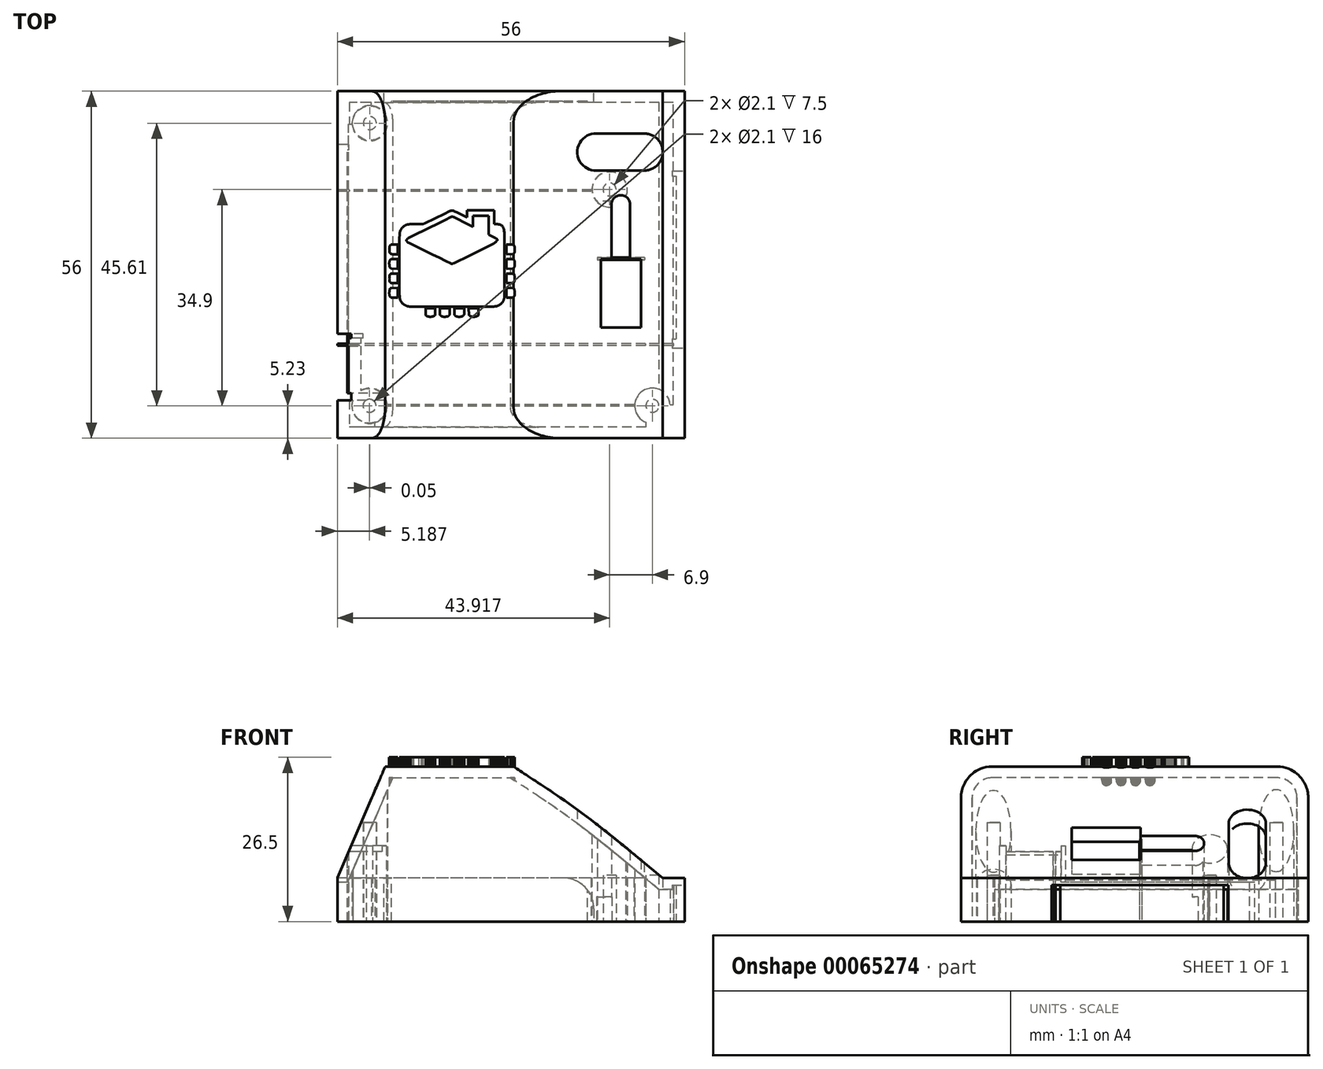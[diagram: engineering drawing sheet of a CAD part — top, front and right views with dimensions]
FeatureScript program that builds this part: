
annotation { "Feature Type Name" : "Feature", "Feature Type Description" : "" }
export const myFeature = defineFeature(function(context is Context, id is Id, definition is map)
    precondition{}
    {
        {
            var Q0;
            Q0=qCreatedBy(makeId("Top.planeOp"),FACE);
            var sketch = newSketch(context, id + "F0", { "sketchPlane" : qUnion([Q0])});
            skLineSegment(sketch, "E0.rect.bottom", {"start": v(22.84, -21.13) * mm, "end": v(-26.83, -21.13) * mm});
            skLineSegment(sketch, "E0.rect.top", {"start": v(22.84, 28.7) * mm, "end": v(-26.83, 28.7) * mm});
            skLineSegment(sketch, "E0.rect.left", {"start": v(22.84, -21.13) * mm, "end": v(22.84, 28.7) * mm});
            skPoint(sketch, "E0.rect.middle", {"position": v(-2, 3.78) * mm});
            skCircle(sketch, "E1", {"center": v(-24.81, -18.99) * mm, "radius": 1.05 * mm});
            skCircle(sketch, "E2", {"center": v(-24.76, 26.62) * mm, "radius": 1.05 * mm});
            skCircle(sketch, "E3", {"center": v(13.92, 15.91) * mm, "radius": 1.05 * mm});
            skLineSegment(sketch, "E4", {"start": v(-2, -21.13) * mm, "end": v(-2, -18.21) * mm});
            skCircle(sketch, "E5.MirrorC", {"center": v(20.82, -18.99) * mm, "radius": 1.05 * mm});
            skLineSegment(sketch, "E6.rect.bottom", {"start": v(24.75, -22.97) * mm, "end": v(-28.75, -22.97) * mm});
            skLineSegment(sketch, "E6.rect.top", {"start": v(24.75, 30.53) * mm, "end": v(-28.75, 30.53) * mm});
            skLineSegment(sketch, "E6.rect.left", {"start": v(24.75, -22.97) * mm, "end": v(24.75, 30.53) * mm});
            skLineSegment(sketch, "E6.rect.right", {"start": v(-28.75, -22.97) * mm, "end": v(-28.75, 30.53) * mm});
            skLineSegment(sketch, "E7.rect.bottom", {"start": v(26, -24.22) * mm, "end": v(-30, -24.22) * mm});
            skLineSegment(sketch, "E7.rect.top", {"start": v(26, 31.78) * mm, "end": v(-30, 31.78) * mm});
            skLineSegment(sketch, "E7.rect.left", {"start": v(26, -24.22) * mm, "end": v(26, 31.78) * mm});
            skLineSegment(sketch, "E7.rect.right", {"start": v(-30, -24.22) * mm, "end": v(-30, 31.78) * mm});
            skPoint(sketch, "E8", {"position": v(8.65, 14) * mm});
            skSolve(sketch);
        }
        {
            var Q0;
            Q0=qSketchRegion(id+"F0",true);
            var Q1;
            Q1=makeQuery(id+"F0.imprint","IMPRINT",FACE,{"disambiguationData":[TD([[makeQuery(id+"F0.imprint","IMPRINT",EDGE,{"derivedFrom":sQuery(id+"F0.wireOp",EDGE,"E1")}),-1.0]])]});
            extrude(context, id + "F1", {"entities" : qUnion([Q0, Q1]), "depth" : 25 * mm});
        }
        {
            var Q0;
            Q0=qCreatedBy(makeId("Front.planeOp"),FACE);
            var sketch = newSketch(context, id + "F2", { "sketchPlane" : qUnion([Q0])});
            skLineSegment(sketch, "E9", {"start": v(0, 0) * mm, "end": v(0, 7) * mm});
            skLineSegment(sketch, "E10", {"start": v(0, 7) * mm, "end": v(26.03, 7) * mm});
            skLineSegment(sketch, "E11", {"start": v(26.03, 7) * mm, "end": v(26.03, 25.51) * mm});
            skLineSegment(sketch, "E12", {"start": v(15.3, 7) * mm, "end": v(26.03, 7) * mm});
            skLineSegment(sketch, "E13", {"start": v(0, 7) * mm, "end": v(-30.02, 7) * mm});
            skLineSegment(sketch, "E14", {"start": v(-30.02, 7) * mm, "end": v(-22.06, 25.51) * mm});
            skLineSegment(sketch, "E15", {"start": v(-22.06, 25.51) * mm, "end": v(-2.39, 25.51) * mm});
            skFitSpline(sketch, "E16", {"points": [v(-2.39, 25.51) * mm, v(9.33, 17.59) * mm, v(22.47, 7) * mm], "startDerivative": vector(24.35, -15.7) * mm, "endDerivative": vector(25.35, -21.24) * mm});
            skLineSegment(sketch, "E17", {"start": v(26.03, 25.51) * mm, "end": v(-2.39, 25.51) * mm});
            skLineSegment(sketch, "E18", {"start": v(-22.06, 25.51) * mm, "end": v(-30.02, 25.51) * mm});
            skLineSegment(sketch, "E19", {"start": v(-30.02, 25.51) * mm, "end": v(-30.02, 7) * mm});
            skSolve(sketch);
        }
        {
            var Q0;
            Q0=makeQuery(id+"F2.imprint","IMPRINT",FACE,{"disambiguationData":[TD([[makeQuery(id+"F2.imprint","IMPRINT",EDGE,{"derivedFrom":sQuery(id+"F2.wireOp",EDGE,"E14")}),1.0]])]});
            var Q1;
            {var subQ0=sQuery(id+"F2.wireOp",EDGE,"E11");Q1=makeQuery(id+"F2.imprint","IMPRINT",FACE,{"disambiguationData":[TD([[makeQuery(id+"F2.imprint","IMPRINT",EDGE,{"derivedFrom":subQ0}),1.0]])]});}
            extrude(context, id + "F3", {"entities" : qUnion([Q0, Q1]), "operationType" : NewBodyOperationType.REMOVE, "endBound" : BoundingType.UP_TO_NEXT, "oppositeDirection" : true, "depth" : 25 * mm, "hasSecondDirection" : true, "secondDirectionOppositeDirection" : false, "secondDirectionDepth" : 25 * mm});
        }
        {
            var Q0;
            Q0=makeQuery(id+"F1.opExtrude","CAP_EDGE",EDGE,{"disambiguationData":[OSD([sQuery(id+"F0.wireOp",EDGE,"E7.rect.right")])],"isStart":false});
            var Q1;
            Q1=makeQuery(id+"F3.boolean.opBoolean","COPY",EDGE,{"derivedFrom":makeQuery(id+"F3.opExtrude","TWEAK_EDGE",EDGE,{"derivedFrom":[makeQuery(id+"F1.opExtrude","CAP_FACE",FACE,{"disambiguationData":[OSD([sQuery(id+"F0.wireOp",EDGE,"E1"),sQuery(id+"F0.wireOp",EDGE,"E2"),sQuery(id+"F0.wireOp",EDGE,"E3"),sQuery(id+"F0.wireOp",EDGE,"E5.MirrorC"),sQuery(id+"F0.wireOp",EDGE,"E7.rect.bottom"),sQuery(id+"F0.wireOp",EDGE,"E7.rect.top"),sQuery(id+"F0.wireOp",EDGE,"E7.rect.left"),sQuery(id+"F0.wireOp",EDGE,"E7.rect.right")])],"isStart":false}),makeQuery(id+"F2.imprint","IMPRINT",EDGE,{"derivedFrom":sQuery(id+"F2.wireOp",EDGE,"ff17f17f-c23f-4b7b-92e3-773d52701edb")})]})});
            var Q2;
            Q2=makeQuery(id+"F3.boolean.opBoolean","COPY",EDGE,{"derivedFrom":makeQuery(id+"F3.opExtrude","TWEAK_EDGE",EDGE,{"derivedFrom":[makeQuery(id+"F1.opExtrude","CAP_FACE",FACE,{"disambiguationData":[OSD([sQuery(id+"F0.wireOp",EDGE,"E1"),sQuery(id+"F0.wireOp",EDGE,"E2"),sQuery(id+"F0.wireOp",EDGE,"E3"),sQuery(id+"F0.wireOp",EDGE,"E5.MirrorC"),sQuery(id+"F0.wireOp",EDGE,"E7.rect.bottom"),sQuery(id+"F0.wireOp",EDGE,"E7.rect.top"),sQuery(id+"F0.wireOp",EDGE,"E7.rect.left"),sQuery(id+"F0.wireOp",EDGE,"E7.rect.right")])],"isStart":false}),makeQuery(id+"F2.imprint","IMPRINT",EDGE,{"derivedFrom":sQuery(id+"F2.wireOp",EDGE,"7c30f75c-de24-4105-9ec6-0528e7197d9e")})]})});
            var Q3;
            {var subQ0=sQuery(id+"F2.wireOp",EDGE,"cpQ2IQLn-lepx-jHqE-Occg-QwCyzWVKbBFz");var subQ1=sQuery(id+"F2.wireOp",EDGE,"9136473a-ce9f-4df1-8e41-d79c079f6f02");var subQ2=makeQuery(id+"F2.imprint","INTERSECT",VERTEX,{"disambiguationData":[OD(0.0)],"derivedFrom":[subQ1,subQ0]});var subQ4=makeQuery(id+"F2.imprint","INTERSECT",VERTEX,{"disambiguationData":[OD(1.0)],"derivedFrom":[subQ1,subQ0]});Q3=makeQuery(id+"F3.boolean.opBoolean","COPY",EDGE,{"derivedFrom":makeQuery(id+"F3.opExtrude","TWEAK_EDGE",EDGE,{"derivedFrom":[makeQuery(id+"F1.opExtrude","CAP_FACE",FACE,{"disambiguationData":[OSD([sQuery(id+"F0.wireOp",EDGE,"E1"),sQuery(id+"F0.wireOp",EDGE,"E2"),sQuery(id+"F0.wireOp",EDGE,"E3"),sQuery(id+"F0.wireOp",EDGE,"E5.MirrorC"),sQuery(id+"F0.wireOp",EDGE,"E7.rect.bottom"),sQuery(id+"F0.wireOp",EDGE,"E7.rect.top"),sQuery(id+"F0.wireOp",EDGE,"E7.rect.left"),sQuery(id+"F0.wireOp",EDGE,"E7.rect.right")])],"isStart":false}),makeQuery(id+"F2.imprint","IMPRINT",EDGE,{"disambiguationData":[TD([[subQ4,1.0]])],"derivedFrom":subQ0}),makeQuery(id+"F2.imprint","IMPRINT",EDGE,{"disambiguationData":[TD([[subQ2,1.0]])],"derivedFrom":subQ0}),makeQuery(id+"F2.imprint","IMPRINT",EDGE,{"disambiguationData":[TD([[subQ2,-1.0]])],"derivedFrom":subQ0})]})});}
            var Q4;
            {var subQ0=sQuery(id+"F2.wireOp",EDGE,"cpQ2IQLn-lepx-jHqE-Occg-QwCyzWVKbBFz");var subQ1=sQuery(id+"F2.wireOp",EDGE,"9136473a-ce9f-4df1-8e41-d79c079f6f02");var subQ2=makeQuery(id+"F2.imprint","INTERSECT",VERTEX,{"disambiguationData":[OD(0.0)],"derivedFrom":[subQ1,subQ0]});var subQ3=sQuery(id+"F2.wireOp",EDGE,"7c30f75c-de24-4105-9ec6-0528e7197d9e");var subQ4=makeQuery(id+"F2.imprint","INTERSECT",VERTEX,{"derivedFrom":[subQ3,subQ0]});var subQ5=makeQuery(id+"F2.imprint","INTERSECT",VERTEX,{"disambiguationData":[OD(1.0)],"derivedFrom":[subQ1,subQ0]});Q4=makeQuery(id+"F3.boolean.opBoolean","COPY",EDGE,{"derivedFrom":makeQuery(id+"F3.opExtrude","TWEAK_EDGE",EDGE,{"disambiguationData":[OD(0.0)],"derivedFrom":[makeQuery(id+"F2.imprint","IMPRINT",EDGE,{"disambiguationData":[TD([[subQ4,1.0]])],"derivedFrom":subQ3}),makeQuery(id+"F2.imprint","IMPRINT",EDGE,{"disambiguationData":[TD([[subQ5,1.0]])],"derivedFrom":subQ0}),makeQuery(id+"F2.imprint","IMPRINT",EDGE,{"disambiguationData":[TD([[subQ2,1.0]])],"derivedFrom":subQ0}),makeQuery(id+"F2.imprint","IMPRINT",EDGE,{"disambiguationData":[TD([[subQ2,-1.0]])],"derivedFrom":subQ0})]})});}
            var Q5;
            {var subQ0=sQuery(id+"F2.wireOp",EDGE,"cpQ2IQLn-lepx-jHqE-Occg-QwCyzWVKbBFz");var subQ1=sQuery(id+"F2.wireOp",EDGE,"9136473a-ce9f-4df1-8e41-d79c079f6f02");var subQ2=makeQuery(id+"F2.imprint","INTERSECT",VERTEX,{"disambiguationData":[OD(0.0)],"derivedFrom":[subQ1,subQ0]});var subQ3=sQuery(id+"F2.wireOp",EDGE,"7c30f75c-de24-4105-9ec6-0528e7197d9e");var subQ4=makeQuery(id+"F2.imprint","INTERSECT",VERTEX,{"derivedFrom":[subQ3,subQ0]});var subQ5=makeQuery(id+"F2.imprint","INTERSECT",VERTEX,{"disambiguationData":[OD(1.0)],"derivedFrom":[subQ1,subQ0]});Q5=makeQuery(id+"F3.boolean.opBoolean","COPY",EDGE,{"derivedFrom":makeQuery(id+"F3.opExtrude","TWEAK_EDGE",EDGE,{"disambiguationData":[OD(1.0)],"derivedFrom":[makeQuery(id+"F2.imprint","IMPRINT",EDGE,{"disambiguationData":[TD([[subQ4,1.0]])],"derivedFrom":subQ3}),makeQuery(id+"F2.imprint","IMPRINT",EDGE,{"disambiguationData":[TD([[subQ5,1.0]])],"derivedFrom":subQ0}),makeQuery(id+"F2.imprint","IMPRINT",EDGE,{"disambiguationData":[TD([[subQ2,1.0]])],"derivedFrom":subQ0}),makeQuery(id+"F2.imprint","IMPRINT",EDGE,{"disambiguationData":[TD([[subQ2,-1.0]])],"derivedFrom":subQ0})]})});}
            var Q6;
            Q6=makeQuery(id+"F1.opExtrude","CAP_EDGE",EDGE,{"disambiguationData":[OSD([sQuery(id+"F0.wireOp",EDGE,"E7.rect.bottom")])],"isStart":false});
            var Q7;
            {var subQ0=sQuery(id+"F2.wireOp",EDGE,"cpQ2IQLn-lepx-jHqE-Occg-QwCyzWVKbBFz");var subQ1=sQuery(id+"F2.wireOp",EDGE,"9136473a-ce9f-4df1-8e41-d79c079f6f02");var subQ2=makeQuery(id+"F2.imprint","INTERSECT",VERTEX,{"disambiguationData":[OD(0.0)],"derivedFrom":[subQ1,subQ0]});var subQ4=makeQuery(id+"F2.imprint","INTERSECT",VERTEX,{"disambiguationData":[OD(1.0)],"derivedFrom":[subQ1,subQ0]});Q7=makeQuery(id+"F3.boolean.opBoolean","COPY",EDGE,{"derivedFrom":makeQuery(id+"F3.opExtrude","TWEAK_EDGE",EDGE,{"derivedFrom":[makeQuery(id+"F1.opExtrude","SWEPT_FACE",FACE,{"disambiguationData":[OSD([sQuery(id+"F0.wireOp",EDGE,"E7.rect.bottom")])]}),makeQuery(id+"F2.imprint","IMPRINT",EDGE,{"disambiguationData":[TD([[subQ4,1.0]])],"derivedFrom":subQ0}),makeQuery(id+"F2.imprint","IMPRINT",EDGE,{"disambiguationData":[TD([[subQ2,1.0]])],"derivedFrom":subQ0}),makeQuery(id+"F2.imprint","IMPRINT",EDGE,{"disambiguationData":[TD([[subQ2,-1.0]])],"derivedFrom":subQ0})]})});}
            var Q8;
            Q8=makeQuery(id+"F1.opExtrude","CAP_EDGE",EDGE,{"disambiguationData":[OSD([sQuery(id+"F0.wireOp",EDGE,"E7.rect.top")])],"isStart":false});
            var Q9;
            {var subQ0=sQuery(id+"F2.wireOp",EDGE,"cpQ2IQLn-lepx-jHqE-Occg-QwCyzWVKbBFz");var subQ1=sQuery(id+"F2.wireOp",EDGE,"9136473a-ce9f-4df1-8e41-d79c079f6f02");var subQ2=makeQuery(id+"F2.imprint","INTERSECT",VERTEX,{"disambiguationData":[OD(0.0)],"derivedFrom":[subQ1,subQ0]});var subQ4=makeQuery(id+"F2.imprint","INTERSECT",VERTEX,{"disambiguationData":[OD(1.0)],"derivedFrom":[subQ1,subQ0]});Q9=makeQuery(id+"F3.boolean.opBoolean","COPY",EDGE,{"derivedFrom":makeQuery(id+"F3.opExtrude","TWEAK_EDGE",EDGE,{"derivedFrom":[makeQuery(id+"F1.opExtrude","SWEPT_FACE",FACE,{"disambiguationData":[OSD([sQuery(id+"F0.wireOp",EDGE,"E7.rect.top")])]}),makeQuery(id+"F2.imprint","IMPRINT",EDGE,{"disambiguationData":[TD([[subQ4,1.0]])],"derivedFrom":subQ0}),makeQuery(id+"F2.imprint","IMPRINT",EDGE,{"disambiguationData":[TD([[subQ2,1.0]])],"derivedFrom":subQ0}),makeQuery(id+"F2.imprint","IMPRINT",EDGE,{"disambiguationData":[TD([[subQ2,-1.0]])],"derivedFrom":subQ0})]})});}
            var Q10;
            Q10=makeQuery(id+"F3.boolean.opBoolean","COPY",EDGE,{"derivedFrom":makeQuery(id+"F3.opExtrude","CAP_EDGE",EDGE,{"disambiguationData":[OSD([sQuery(id+"F2.wireOp",EDGE,"E16")]),topologyDisambiguationEdgeConnected([makeQuery(id+"F1.opExtrude","CAP_FACE",FACE,{"disambiguationData":[OSD([sQuery(id+"F0.wireOp",EDGE,"E1"),sQuery(id+"F0.wireOp",EDGE,"E2"),sQuery(id+"F0.wireOp",EDGE,"E3"),sQuery(id+"F0.wireOp",EDGE,"E5.MirrorC"),sQuery(id+"F0.wireOp",EDGE,"E7.rect.bottom"),sQuery(id+"F0.wireOp",EDGE,"E7.rect.top"),sQuery(id+"F0.wireOp",EDGE,"E7.rect.left"),sQuery(id+"F0.wireOp",EDGE,"E7.rect.right")])],"isStart":false})])],"isStart":false})});
            var Q11;
            {var subQ0=sQuery(id+"F2.wireOp",EDGE,"E14");Q11=makeQuery(id+"F3.boolean.opBoolean","COPY",EDGE,{"derivedFrom":makeQuery(id+"F3.opExtrude","CAP_EDGE",EDGE,{"disambiguationData":[OSD([subQ0]),topologyDisambiguationEdgeConnected([makeQuery(id+"F1.opExtrude","CAP_FACE",FACE,{"disambiguationData":[OSD([sQuery(id+"F0.wireOp",EDGE,"E1"),sQuery(id+"F0.wireOp",EDGE,"E2"),sQuery(id+"F0.wireOp",EDGE,"E3"),sQuery(id+"F0.wireOp",EDGE,"E5.MirrorC"),sQuery(id+"F0.wireOp",EDGE,"E7.rect.bottom"),sQuery(id+"F0.wireOp",EDGE,"E7.rect.top"),sQuery(id+"F0.wireOp",EDGE,"E7.rect.left"),sQuery(id+"F0.wireOp",EDGE,"E7.rect.right")])],"isStart":false})])],"isStart":false})});}
            fillet(context, id + "F4", {"entities" : qUnion([Q0, Q1, Q2, Q3, Q4, Q5, Q6, Q7, Q8, Q9, Q10, Q11]), "radius" : 5 * mm, "tangentPropagation" : true, "allowEdgeOverflow" : false});
        }
        {
            var Q0;
            Q0=makeQuery(id+"F1.opExtrude","SWEPT_BODY",BODY,{"disambiguationData":[OSD([sQuery(id+"F0.wireOp",EDGE,"E1"),sQuery(id+"F0.wireOp",EDGE,"E2"),sQuery(id+"F0.wireOp",EDGE,"E3"),sQuery(id+"F0.wireOp",EDGE,"E5.MirrorC"),sQuery(id+"F0.wireOp",EDGE,"E7.rect.bottom"),sQuery(id+"F0.wireOp",EDGE,"E7.rect.top"),sQuery(id+"F0.wireOp",EDGE,"E7.rect.left"),sQuery(id+"F0.wireOp",EDGE,"E7.rect.right")])]});
            transform(context, id + "F5", {"entities" : qUnion([Q0]), "transformType" : TransformType.TRANSLATION_3D, "dx" : -5 * mm, "dy" : -12 * mm, "dz" : 0 * mm, "makeCopy" : false});
        }
        {
            var Q0;
            Q0=makeQuery(id+"F1.opExtrude","CAP_FACE",FACE,{"disambiguationData":[OSD([sQuery(id+"F0.wireOp",EDGE,"E1"),sQuery(id+"F0.wireOp",EDGE,"E2"),sQuery(id+"F0.wireOp",EDGE,"E3"),sQuery(id+"F0.wireOp",EDGE,"E5.MirrorC"),sQuery(id+"F0.wireOp",EDGE,"E7.rect.bottom"),sQuery(id+"F0.wireOp",EDGE,"E7.rect.top"),sQuery(id+"F0.wireOp",EDGE,"E7.rect.left"),sQuery(id+"F0.wireOp",EDGE,"E7.rect.right")])],"isStart":true});
            shell(context, id + "F6", {"entities" : qUnion([Q0]), "thickness" : 1.8 * mm});
        }
        {
            var Q0;
            Q0=makeQuery(id+"F1.opExtrude","SWEPT_FACE",FACE,{"disambiguationData":[OSD([sQuery(id+"F0.wireOp",EDGE,"E7.rect.left")])]});
            cPlane(context, id + "F7", {"entities" : qUnion([Q0]), "cplaneType" : CPlaneType.OFFSET, "offset" : 0 * mm, "width" : 150 * mm, "height" : 150 * mm});
        }
        {
            var Q0;
            Q0=qCreatedBy(id+"F7.planeOp",FACE);
            var sketch = newSketch(context, id + "F8", { "sketchPlane" : qUnion([Q0])});
            skLineSegment(sketch, "E20.bottom", {"start": v(6.92, 0) * mm, "end": v(-20.2, 0) * mm});
            skLineSegment(sketch, "E20.top", {"start": v(6.92, 5.87) * mm, "end": v(-20.2, 5.87) * mm});
            skLineSegment(sketch, "E21", {"start": v(-20.2, 5.87) * mm, "end": v(-21.64, 5.87) * mm});
            skLineSegment(sketch, "E22", {"start": v(-21.64, 5.87) * mm, "end": v(-21.64, 0) * mm});
            skLineSegment(sketch, "E23", {"start": v(-21.64, 0) * mm, "end": v(-20.2, 0) * mm});
            skLineSegment(sketch, "E24", {"start": v(-20.2, 5.87) * mm, "end": v(-20.2, 0) * mm});
            skLineSegment(sketch, "E25", {"start": v(6.92, 0) * mm, "end": v(6.92, 5.87) * mm});
            skLineSegment(sketch, "E26", {"start": v(6.12, 5.87) * mm, "end": v(6.12, 0) * mm});
            skPoint(sketch, "E27.orphan", {"position": v(7.84, 0) * mm});
            skSolve(sketch);
        }
        {
            var Q0;
            Q0=qSketchRegion(id+"F8",true);
            extrude(context, id + "F9", {"entities" : qUnion([Q0]), "operationType" : NewBodyOperationType.REMOVE, "oppositeDirection" : true, "depth" : (1.7 - 0.3) * mm});
        }
        {
            var Q0;
            Q0=makeQuery(id+"F8.imprint","IMPRINT",FACE,{"disambiguationData":[TD([[makeQuery(id+"F8.imprint","IMPRINT",EDGE,{"derivedFrom":sQuery(id+"F8.wireOp",EDGE,"E21")}),1.0]])]});
            var Q1;
            {var subQ0=sQuery(id+"F8.wireOp",EDGE,"E20.left");Q1=makeQuery(id+"F8.imprint","IMPRINT",FACE,{"disambiguationData":[TD([[makeQuery(id+"F8.imprint","IMPRINT",EDGE,{"derivedFrom":subQ0}),1.0]])]});}
            var Q2;
            {var subQ0=sQuery(id+"F8.wireOp",EDGE,"E25");Q2=makeQuery(id+"F8.imprint","IMPRINT",FACE,{"disambiguationData":[TD([[makeQuery(id+"F8.imprint","IMPRINT",EDGE,{"derivedFrom":subQ0}),1.0]])]});}
            extrude(context, id + "F10", {"entities" : qUnion([Q0, Q1, Q2]), "operationType" : NewBodyOperationType.REMOVE, "oppositeDirection" : true, "depth" : 2 * mm});
        }
        {
            var Q0;
            Q0=makeQuery(id+"F1.opExtrude","SWEPT_FACE",FACE,{"disambiguationData":[OSD([sQuery(id+"F0.wireOp",EDGE,"E7.rect.right")])]});
            cPlane(context, id + "F11", {"entities" : qUnion([Q0]), "cplaneType" : CPlaneType.OFFSET, "offset" : 0 * mm, "width" : 150 * mm, "height" : 150 * mm});
        }
        {
            var Q0;
            Q0=qCreatedBy(id+"F11.planeOp",FACE);
            var sketch = newSketch(context, id + "F12", { "sketchPlane" : qUnion([Q0])});
            skLineSegment(sketch, "E28.top", {"start": v(-11.15, 6.31) * mm, "end": v(19.35, 6.31) * mm});
            skLineSegment(sketch, "E29", {"start": v(27.25, 11.15) * mm, "end": v(27.25, 11.15) * mm});
            skLineSegment(sketch, "E30", {"start": v(19.35, 11.15) * mm, "end": v(19.35, 6.31) * mm});
            skLineSegment(sketch, "E31", {"start": v(30.08, 0) * mm, "end": v(30.08, 11.15) * mm});
            skLineSegment(sketch, "E32", {"start": v(-11.15, 0) * mm, "end": v(-11.15, 6.31) * mm});
            skPoint(sketch, "E33.start.orphan", {"position": v(-15.15, 0) * mm});
            skLineSegment(sketch, "E34", {"start": v(30.08, 0) * mm, "end": v(-11.15, 0) * mm});
            skLineSegment(sketch, "E35", {"start": v(-10.29, 6.31) * mm, "end": v(-10.29, 0) * mm});
            skLineSegment(sketch, "E36", {"start": v(28.97, 0) * mm, "end": v(28.97, 11.15) * mm});
            skLineSegment(sketch, "E37", {"start": v(19.35, 6.31) * mm, "end": v(20.08, 6.31) * mm});
            skLineSegment(sketch, "E38", {"start": v(20.08, 6.31) * mm, "end": v(20.08, 11.15) * mm});
            skLineSegment(sketch, "E39", {"start": v(19.35, 11.15) * mm, "end": v(19.35, 12.2) * mm});
            skLineSegment(sketch, "E40", {"start": v(19.35, 12.2) * mm, "end": v(30.08, 12.2) * mm});
            skLineSegment(sketch, "E41", {"start": v(30.08, 12.2) * mm, "end": v(30.08, 11.15) * mm});
            skLineSegment(sketch, "E42", {"start": v(28.97, 11.15) * mm, "end": v(28.97, 12.2) * mm});
            skLineSegment(sketch, "E43", {"start": v(20.08, 11.15) * mm, "end": v(20.08, 12.2) * mm});
            skSolve(sketch);
        }
        {
            var Q0;
            {var subQ0=sQuery(id+"F12.wireOp",EDGE,"E32");Q0=makeQuery(id+"F12.imprint","IMPRINT",FACE,{"disambiguationData":[TD([[makeQuery(id+"F12.imprint","IMPRINT",EDGE,{"derivedFrom":subQ0}),-1.0]])]});}
            var Q1;
            {var subQ1=sQuery(id+"F12.wireOp",EDGE,"E35");Q1=makeQuery(id+"F12.imprint","IMPRINT",FACE,{"disambiguationData":[TD([[makeQuery(id+"F12.imprint","IMPRINT",EDGE,{"derivedFrom":subQ1}),1.0]])]});}
            var Q2;
            Q2=makeQuery(id+"F12.imprint","IMPRINT",FACE,{"disambiguationData":[TD([[makeQuery(id+"F12.imprint","IMPRINT",EDGE,{"derivedFrom":sQuery(id+"F12.wireOp",EDGE,"E30")}),1.0]])]});
            extrude(context, id + "F13", {"entities" : qUnion([Q0, Q1, Q2]), "operationType" : NewBodyOperationType.REMOVE, "oppositeDirection" : true, "depth" : 1.6 * mm});
        }
        {
            var Q0;
            {var subQ0=sQuery(id+"F12.wireOp",EDGE,"E32");Q0=makeQuery(id+"F12.imprint","IMPRINT",FACE,{"disambiguationData":[TD([[makeQuery(id+"F12.imprint","IMPRINT",EDGE,{"derivedFrom":subQ0}),-1.0]])]});}
            var Q1;
            {var subQ0=sQuery(id+"F12.wireOp",EDGE,"E30");Q1=makeQuery(id+"F12.imprint","IMPRINT",FACE,{"disambiguationData":[TD([[makeQuery(id+"F12.imprint","IMPRINT",EDGE,{"derivedFrom":subQ0}),1.0]])]});}
            var Q2;
            {var subQ0=sQuery(id+"F12.wireOp",EDGE,"E31");Q2=makeQuery(id+"F12.imprint","IMPRINT",FACE,{"disambiguationData":[TD([[makeQuery(id+"F12.imprint","IMPRINT",EDGE,{"derivedFrom":subQ0}),1.0]])]});}
            extrude(context, id + "F14", {"entities" : qUnion([Q0, Q1, Q2]), "operationType" : NewBodyOperationType.REMOVE, "oppositeDirection" : true, "depth" : 8 * mm});
        }
        {
            var Q0;
            Q0=qCreatedBy(makeId("Top.planeOp"),FACE);
            var sketch = newSketch(context, id + "F15", { "sketchPlane" : qUnion([Q0])});
            skLineSegment(sketch, "E44.bottom", {"start": v(-27.19, -29.45) * mm, "end": v(-33.17, -29.45) * mm});
            skLineSegment(sketch, "E44.top", {"start": v(-27.19, -20) * mm, "end": v(-33.17, -20) * mm});
            skLineSegment(sketch, "E44.left", {"start": v(-27.19, -29.45) * mm, "end": v(-27.19, -21.32) * mm});
            skLineSegment(sketch, "E44.right", {"start": v(-33.17, -29.45) * mm, "end": v(-33.17, -21.32) * mm});
            skLineSegment(sketch, "E45", {"start": v(-33.17, -20.99) * mm, "end": v(-27.19, -20.99) * mm});
            skLineSegment(sketch, "E46", {"start": v(-33.17, -21.32) * mm, "end": v(-27.19, -21.32) * mm});
            skLineSegment(sketch, "E47.trimOffspring", {"start": v(-27.19, -20.99) * mm, "end": v(-27.19, -20) * mm});
            skLineSegment(sketch, "E48.trimOffspring", {"start": v(-33.17, -20.99) * mm, "end": v(-33.17, -20) * mm});
            skSolve(sketch);
        }
        {
            var Q0;
            Q0=qSketchRegion(id+"F15",true);
            var Q1;
            {var subQ5=sQuery(id+"F0.wireOp",EDGE,"E2");var subQ6=sQuery(id+"F2.wireOp",EDGE,"E14");Q1=makeQuery(id+"F14.boolean.opBoolean","SPLIT",FACE,{"disambiguationData":[TD([makeQuery(id+"F6.opShell","OFFSET_FACE",FACE,{"disambiguationData":[OSD([subQ5])]})])],"derivedFrom":makeQuery(id+"F6.opShell","OFFSET_FACE",FACE,{"disambiguationData":[OSD([subQ6])]})});}
            extrude(context, id + "F16", {"entities" : qUnion([Q0]), "operationType" : NewBodyOperationType.REMOVE, "endBoundEntityFace" : qUnion([Q1]), "depth" : 11.3 * mm});
        }
        {
            var Q0;
            Q0=makeQuery(id+"F1.opExtrude","SWEPT_FACE",FACE,{"disambiguationData":[OSD([sQuery(id+"F0.wireOp",EDGE,"E7.rect.top")])]});
            cPlane(context, id + "F17", {"entities" : qUnion([Q0]), "cplaneType" : CPlaneType.OFFSET, "offset" : 0 * mm, "width" : 150 * mm, "height" : 150 * mm});
        }
        {
            var Q0;
            Q0=qCreatedBy(id+"F17.planeOp",FACE);
            var sketch = newSketch(context, id + "F18", { "sketchPlane" : qUnion([Q0])});
            skLineSegment(sketch, "E49.bottom", {"start": v(-6.36, 0) * mm, "end": v(27.5, 0) * mm});
            skLineSegment(sketch, "E49.top", {"start": v(-1.36, 7.05) * mm, "end": v(27.5, 7.05) * mm});
            skLineSegment(sketch, "E49.left", {"start": v(-6.36, 0) * mm, "end": v(-6.36, 2.05) * mm});
            skLineSegment(sketch, "E50", {"start": v(-5.32, 5.11) * mm, "end": v(-5.32, 0) * mm});
            skLineSegment(sketch, "E51", {"start": v(27.5, 7.05) * mm, "end": v(27.5, 0) * mm});
            skLineSegment(sketch, "E52", {"start": v(26.27, 7.05) * mm, "end": v(26.27, 0) * mm});
            skPoint(sketch, "E53.visualSharp", {"position": v(-6.36, 7.05) * mm});
            skArc(sketch, "E53.filletArc", {"start": v(-1.36, 7.05) * mm, "mid": v(-4.9, 5.59) * mm, "end": v(-6.36, 2.05) * mm});
            skSolve(sketch);
        }
        {
            var Q0;
            Q0=qSketchRegion(id+"F18",true);
            extrude(context, id + "F19", {"entities" : qUnion([Q0]), "operationType" : NewBodyOperationType.REMOVE, "oppositeDirection" : true, "depth" : 1.6 * mm});
        }
        {
            var Q0;
            Q0=qCreatedBy(makeId("Top.planeOp"),FACE);
            var sketch = newSketch(context, id + "F20", { "sketchPlane" : qUnion([Q0])});
            skLineSegment(sketch, "E54", {"start": v(12.81, -31.08) * mm, "end": v(12.81, -30.78) * mm});
            skLineSegment(sketch, "E55", {"start": v(19.24, -20.99) * mm, "end": v(19.24, -21.29) * mm});
            skLineSegment(sketch, "E56", {"start": v(5.94, 3.59) * mm, "end": v(5.94, 3.89) * mm});
            skLineSegment(sketch, "E57", {"start": v(19.24, -21.29) * mm, "end": v(-34.98, -21.29) * mm});
            skLineSegment(sketch, "E58", {"start": v(19.24, -20.99) * mm, "end": v(-34.98, -20.99) * mm});
            skLineSegment(sketch, "E59", {"start": v(-34.98, -20.99) * mm, "end": v(-34.98, -21.29) * mm});
            skLineSegment(sketch, "E60", {"start": v(12.81, -31.08) * mm, "end": v(-27.73, -31.08) * mm});
            skLineSegment(sketch, "E61", {"start": v(12.81, -30.78) * mm, "end": v(-27.73, -30.78) * mm});
            skLineSegment(sketch, "E62", {"start": v(5.94, 3.59) * mm, "end": v(-34.95, 3.59) * mm});
            skLineSegment(sketch, "E63", {"start": v(5.94, 3.89) * mm, "end": v(-34.95, 3.89) * mm});
            skLineSegment(sketch, "E64", {"start": v(-34.95, 3.89) * mm, "end": v(-34.95, 3.59) * mm});
            skLineSegment(sketch, "E65.bottom", {"start": v(-33.84, 14.47) * mm, "end": v(-32.16, 14.47) * mm});
            skLineSegment(sketch, "E65.top", {"start": v(-33.84, 18.7) * mm, "end": v(-29.5, 18.7) * mm});
            skLineSegment(sketch, "E65.left", {"start": v(-33.84, 14.47) * mm, "end": v(-33.84, 18.7) * mm});
            skLineSegment(sketch, "E65.right", {"start": v(-29.5, 16.74) * mm, "end": v(-29.5, 18.7) * mm});
            skArc(sketch, "E66", {"start": v(-29.5, 16.74) * mm, "mid": v(-31.35, 16.22) * mm, "end": v(-32.16, 14.47) * mm});
            skLineSegment(sketch, "E67.bottom", {"start": v(-33.6, -31.08) * mm, "end": v(-33.6, -31.08) * mm});
            skLineSegment(sketch, "E67.top", {"start": v(-33.6, -34.81) * mm, "end": v(-31.03, -34.81) * mm});
            skLineSegment(sketch, "E67.left", {"start": v(-33.6, -31.08) * mm, "end": v(-33.6, -34.81) * mm});
            skLineSegment(sketch, "E67.right", {"start": v(-31.03, -31.08) * mm, "end": v(-31.03, -33.21) * mm});
            skLineSegment(sketch, "E68.bottom", {"start": v(-31.03, -34.81) * mm, "end": v(-28.95, -34.81) * mm});
            skLineSegment(sketch, "E68.top", {"start": v(-31.03, -33.21) * mm, "end": v(-28.95, -33.21) * mm});
            skLineSegment(sketch, "E68.right", {"start": v(-28.95, -34.81) * mm, "end": v(-28.95, -33.21) * mm});
            skLineSegment(sketch, "E69", {"start": v(-27.73, -31.08) * mm, "end": v(-27.73, -30.78) * mm});
            skPoint(sketch, "E70.end.orphan", {"position": v(-34.98, -31.08) * mm});
            skPoint(sketch, "E70.start.orphan", {"position": v(-34.98, -30.78) * mm});
            skLineSegment(sketch, "E71.bottom", {"start": v(16.87, -34.88) * mm, "end": v(19.69, -34.88) * mm});
            skLineSegment(sketch, "E71.top", {"start": v(16.87, -30.79) * mm, "end": v(19.69, -30.79) * mm});
            skLineSegment(sketch, "E71.left", {"start": v(16.87, -33.4) * mm, "end": v(16.87, -30.79) * mm});
            skLineSegment(sketch, "E71.right", {"start": v(19.69, -34.88) * mm, "end": v(19.69, -30.79) * mm});
            skLineSegment(sketch, "E72.bottom", {"start": v(16.87, -34.88) * mm, "end": v(14.73, -34.88) * mm});
            skLineSegment(sketch, "E72.top", {"start": v(16.87, -33.4) * mm, "end": v(14.73, -33.4) * mm});
            skLineSegment(sketch, "E72.right", {"start": v(14.73, -34.88) * mm, "end": v(14.73, -33.4) * mm});
            skLineSegment(sketch, "E73.top", {"start": v(-31.03, -30.09) * mm, "end": v(-33.6, -30.09) * mm});
            skLineSegment(sketch, "E73.left", {"start": v(-31.03, -31.08) * mm, "end": v(-31.03, -30.09) * mm});
            skLineSegment(sketch, "E73.right", {"start": v(-33.6, -31.08) * mm, "end": v(-33.6, -30.09) * mm});
            skSolve(sketch);
        }
        {
            var Q0;
            Q0=qSketchRegion(id+"F20",true);
            extrude(context, id + "F21", {"entities" : qUnion([Q0]), "operationType" : NewBodyOperationType.ADD, "depth" : 7 * mm});
        }
        {
            var Q0;
            Q0=qCreatedBy(makeId("Top.planeOp"),FACE);
            var sketch = newSketch(context, id + "F22", { "sketchPlane" : qUnion([Q0])});
            skArc(sketch, "E74", {"start": v(6.16, 2.02) * mm, "mid": v(8.9, 0.56) * mm, "end": v(11.63, 2.02) * mm});
            skLineSegment(sketch, "E75", {"start": v(11.63, 2.02) * mm, "end": v(6.16, 2.02) * mm});
            skSolve(sketch);
        }
        {
            var Q0;
            Q0=qSketchRegion(id+"F22",true);
            extrude(context, id + "F23", {"entities" : qUnion([Q0]), "operationType" : NewBodyOperationType.REMOVE, "depth" : 4 * mm});
        }
        {
            var Q0;
            {var subQ0=sQuery(id+"F18.wireOp",EDGE,"E49.left");Q0=makeQuery(id+"F18.imprint","IMPRINT",FACE,{"disambiguationData":[TD([[makeQuery(id+"F18.imprint","IMPRINT",EDGE,{"derivedFrom":subQ0}),-1.0]])]});}
            var Q1;
            {var subQ0=sQuery(id+"F18.wireOp",EDGE,"E49.right");Q1=makeQuery(id+"F18.imprint","IMPRINT",FACE,{"disambiguationData":[TD([[makeQuery(id+"F18.imprint","IMPRINT",EDGE,{"derivedFrom":subQ0}),1.0]])]});}
            extrude(context, id + "F24", {"entities" : qUnion([Q0, Q1]), "operationType" : NewBodyOperationType.REMOVE, "oppositeDirection" : true, "depth" : 2 * mm});
        }
        {
            var Q0;
            Q0=qCreatedBy(makeId("Top.planeOp"),FACE);
            var sketch = newSketch(context, id + "F25", { "sketchPlane" : qUnion([Q0])});
            skLineSegment(sketch, "E76", {"start": v(21, 19.9) * mm, "end": v(21, 9.52) * mm});
            skLineSegment(sketch, "E77", {"start": v(21, 9.52) * mm, "end": v(17.3, 9.52) * mm});
            skArc(sketch, "E78", {"start": v(9.22, -16.85) * mm, "mid": v(10.72, -18.35) * mm, "end": v(12.22, -16.85) * mm});
            skLineSegment(sketch, "E79", {"start": v(12.22, 0) * mm, "end": v(12.22, -16.85) * mm});
            skLineSegment(sketch, "E80", {"start": v(9.22, 0) * mm, "end": v(9.22, -16.85) * mm});
            skLineSegment(sketch, "E81", {"start": v(9.22, 0) * mm, "end": v(9.22, 1.5) * mm});
            skLineSegment(sketch, "E82", {"start": v(12.22, 0) * mm, "end": v(12.22, 1.5) * mm});
            skArc(sketch, "E83.trimOffspring", {"start": v(12.22, 1.5) * mm, "mid": v(10.72, 3) * mm, "end": v(9.22, 1.5) * mm});
            skPoint(sketch, "E84.center.orphan", {"position": v(10.72, 0) * mm});
            skArc(sketch, "E85", {"start": v(14.47, 6.98) * mm, "mid": v(17.49, 9.95) * mm, "end": v(14.5, 12.95) * mm});
            skArc(sketch, "E86", {"start": v(6.7, 12.96) * mm, "mid": v(3.7, 9.96) * mm, "end": v(6.7, 6.96) * mm});
            skLineSegment(sketch, "E87", {"start": v(14.5, 12.95) * mm, "end": v(6.7, 12.96) * mm});
            skLineSegment(sketch, "E88", {"start": v(6.7, 6.96) * mm, "end": v(14.54, 6.98) * mm});
            skLineSegment(sketch, "E89.rect.bottom", {"start": v(7.48, -18.35) * mm, "end": v(13.95, -18.35) * mm});
            skLineSegment(sketch, "E89.rect.top", {"start": v(7.48, -7.29) * mm, "end": v(13.95, -7.29) * mm});
            skLineSegment(sketch, "E89.rect.left", {"start": v(7.48, -18.35) * mm, "end": v(7.48, -7.29) * mm});
            skLineSegment(sketch, "E89.rect.right", {"start": v(13.95, -18.35) * mm, "end": v(13.95, -7.29) * mm});
            skPoint(sketch, "E89.rect.middle", {"position": v(10.72, -12.82) * mm});
            skPoint(sketch, "E89.rect.cornerSnap0", {"position": v(10.72, -18.35) * mm});
            skSolve(sketch);
        }
        {
            var Q0;
            Q0=qSketchRegion(id+"F25",true);
            extrude(context, id + "F26", {"entities" : qUnion([Q0]), "operationType" : NewBodyOperationType.REMOVE, "depth" : 25 * mm});
        }
        {
            var Q0;
            Q0=qCreatedBy(makeId("Top.planeOp"),FACE);
            var sketch = newSketch(context, id + "F27", { "sketchPlane" : qUnion([Q0])});
            skLineSegment(sketch, "E90", {"start": v(-14.06, 0.58) * mm, "end": v(-9.7, 0.57) * mm});
            skLineSegment(sketch, "E91", {"start": v(-8.04, -3.57) * mm, "end": v(-8.03, -3.84) * mm});
            skLineSegment(sketch, "E92", {"start": v(-8.03, -3.84) * mm, "end": v(-8.04, -13.15) * mm});
            skLineSegment(sketch, "E93", {"start": v(-8.04, -13.15) * mm, "end": v(-8.03, -13.22) * mm});
            skLineSegment(sketch, "E94", {"start": v(-8.03, -13.22) * mm, "end": v(-8.03, -13.28) * mm});
            skLineSegment(sketch, "E95", {"start": v(-8.03, -13.28) * mm, "end": v(-8.04, -13.35) * mm});
            skLineSegment(sketch, "E96", {"start": v(-8.04, -13.35) * mm, "end": v(-8.04, -13.42) * mm});
            skLineSegment(sketch, "E97", {"start": v(-8.04, -13.42) * mm, "end": v(-8.05, -13.48) * mm});
            skLineSegment(sketch, "E98", {"start": v(-8.05, -13.48) * mm, "end": v(-8.06, -13.55) * mm});
            skLineSegment(sketch, "E99", {"start": v(-8.06, -13.55) * mm, "end": v(-8.07, -13.61) * mm});
            skLineSegment(sketch, "E100", {"start": v(-8.07, -13.61) * mm, "end": v(-8.1, -13.68) * mm});
            skLineSegment(sketch, "E101", {"start": v(-8.1, -13.68) * mm, "end": v(-8.1, -13.74) * mm});
            skLineSegment(sketch, "E102", {"start": v(-8.1, -13.74) * mm, "end": v(-8.13, -13.8) * mm});
            skLineSegment(sketch, "E103", {"start": v(-8.13, -13.8) * mm, "end": v(-8.15, -13.86) * mm});
            skLineSegment(sketch, "E104", {"start": v(-8.15, -13.86) * mm, "end": v(-8.18, -13.93) * mm});
            skLineSegment(sketch, "E105", {"start": v(-8.18, -13.93) * mm, "end": v(-8.2, -13.99) * mm});
            skLineSegment(sketch, "E106", {"start": v(-8.2, -13.99) * mm, "end": v(-8.23, -14.05) * mm});
            skLineSegment(sketch, "E107", {"start": v(-8.23, -14.05) * mm, "end": v(-8.26, -14.1) * mm});
            skLineSegment(sketch, "E108", {"start": v(-8.26, -14.1) * mm, "end": v(-8.3, -14.16) * mm});
            skLineSegment(sketch, "E109", {"start": v(-8.3, -14.16) * mm, "end": v(-8.33, -14.22) * mm});
            skLineSegment(sketch, "E110", {"start": v(-8.33, -14.22) * mm, "end": v(-8.37, -14.27) * mm});
            skLineSegment(sketch, "E111", {"start": v(-8.37, -14.27) * mm, "end": v(-8.4, -14.32) * mm});
            skLineSegment(sketch, "E112", {"start": v(-8.4, -14.32) * mm, "end": v(-8.45, -14.37) * mm});
            skLineSegment(sketch, "E113", {"start": v(-8.45, -14.37) * mm, "end": v(-8.5, -14.42) * mm});
            skLineSegment(sketch, "E114", {"start": v(-8.5, -14.42) * mm, "end": v(-8.54, -14.47) * mm});
            skLineSegment(sketch, "E115", {"start": v(-8.54, -14.47) * mm, "end": v(-8.59, -14.52) * mm});
            skLineSegment(sketch, "E116", {"start": v(-8.59, -14.52) * mm, "end": v(-8.63, -14.56) * mm});
            skLineSegment(sketch, "E117", {"start": v(-8.63, -14.56) * mm, "end": v(-8.69, -14.6) * mm});
            skLineSegment(sketch, "E118", {"start": v(-8.69, -14.6) * mm, "end": v(-8.74, -14.64) * mm});
            skLineSegment(sketch, "E119", {"start": v(-8.74, -14.64) * mm, "end": v(-8.8, -14.68) * mm});
            skLineSegment(sketch, "E120", {"start": v(-8.8, -14.68) * mm, "end": v(-8.85, -14.72) * mm});
            skLineSegment(sketch, "E121", {"start": v(-8.85, -14.72) * mm, "end": v(-8.9, -14.75) * mm});
            skLineSegment(sketch, "E122", {"start": v(-8.9, -14.75) * mm, "end": v(-8.95, -14.77) * mm});
            skLineSegment(sketch, "E123", {"start": v(-8.95, -14.77) * mm, "end": v(-8.99, -14.8) * mm});
            skLineSegment(sketch, "E124", {"start": v(-8.99, -14.8) * mm, "end": v(-9.03, -14.81) * mm});
            skLineSegment(sketch, "E125", {"start": v(-9.03, -14.81) * mm, "end": v(-9.07, -14.83) * mm});
            skLineSegment(sketch, "E126", {"start": v(-9.07, -14.83) * mm, "end": v(-9.11, -14.85) * mm});
            skLineSegment(sketch, "E127", {"start": v(-9.11, -14.85) * mm, "end": v(-9.16, -14.86) * mm});
            skLineSegment(sketch, "E128", {"start": v(-9.16, -14.86) * mm, "end": v(-9.2, -14.88) * mm});
            skLineSegment(sketch, "E129", {"start": v(-9.2, -14.88) * mm, "end": v(-9.24, -14.9) * mm});
            skLineSegment(sketch, "E130", {"start": v(-9.24, -14.9) * mm, "end": v(-9.29, -14.9) * mm});
            skLineSegment(sketch, "E131", {"start": v(-9.29, -14.9) * mm, "end": v(-9.33, -14.91) * mm});
            skLineSegment(sketch, "E132", {"start": v(-9.33, -14.91) * mm, "end": v(-9.38, -14.92) * mm});
            skLineSegment(sketch, "E133", {"start": v(-9.38, -14.92) * mm, "end": v(-9.42, -14.93) * mm});
            skLineSegment(sketch, "E134", {"start": v(-9.42, -14.93) * mm, "end": v(-9.51, -14.94) * mm});
            skLineSegment(sketch, "E135", {"start": v(-9.51, -14.94) * mm, "end": v(-9.6, -14.96) * mm});
            skLineSegment(sketch, "E136", {"start": v(-9.6, -14.96) * mm, "end": v(-9.74, -14.97) * mm});
            skLineSegment(sketch, "E137", {"start": v(-9.74, -14.97) * mm, "end": v(-10.2, -14.98) * mm});
            skLineSegment(sketch, "E138", {"start": v(-10.2, -14.98) * mm, "end": v(-23.2, -14.97) * mm});
            skLineSegment(sketch, "E139", {"start": v(-23.2, -14.97) * mm, "end": v(-23.28, -14.97) * mm});
            skLineSegment(sketch, "E140", {"start": v(-23.28, -14.97) * mm, "end": v(-23.35, -14.97) * mm});
            skLineSegment(sketch, "E141", {"start": v(-23.35, -14.97) * mm, "end": v(-23.43, -14.97) * mm});
            skLineSegment(sketch, "E142", {"start": v(-23.43, -14.97) * mm, "end": v(-23.5, -14.96) * mm});
            skLineSegment(sketch, "E143", {"start": v(-23.5, -14.96) * mm, "end": v(-23.58, -14.94) * mm});
            skLineSegment(sketch, "E144", {"start": v(-23.58, -14.94) * mm, "end": v(-23.65, -14.93) * mm});
            skLineSegment(sketch, "E145", {"start": v(-23.65, -14.93) * mm, "end": v(-23.72, -14.9) * mm});
            skLineSegment(sketch, "E146", {"start": v(-23.72, -14.9) * mm, "end": v(-23.8, -14.89) * mm});
            skLineSegment(sketch, "E147", {"start": v(-23.8, -14.89) * mm, "end": v(-23.86, -14.86) * mm});
            skLineSegment(sketch, "E148", {"start": v(-23.86, -14.86) * mm, "end": v(-23.93, -14.83) * mm});
            skLineSegment(sketch, "E149", {"start": v(-23.93, -14.83) * mm, "end": v(-24, -14.8) * mm});
            skLineSegment(sketch, "E150", {"start": v(-24, -14.8) * mm, "end": v(-24.07, -14.77) * mm});
            skLineSegment(sketch, "E151", {"start": v(-24.07, -14.77) * mm, "end": v(-24.13, -14.73) * mm});
            skLineSegment(sketch, "E152", {"start": v(-24.13, -14.73) * mm, "end": v(-24.2, -14.7) * mm});
            skLineSegment(sketch, "E153", {"start": v(-24.2, -14.7) * mm, "end": v(-24.26, -14.65) * mm});
            skLineSegment(sketch, "E154", {"start": v(-24.26, -14.65) * mm, "end": v(-24.32, -14.6) * mm});
            skLineSegment(sketch, "E155", {"start": v(-24.32, -14.6) * mm, "end": v(-24.38, -14.56) * mm});
            skLineSegment(sketch, "E156", {"start": v(-24.38, -14.56) * mm, "end": v(-24.43, -14.51) * mm});
            skLineSegment(sketch, "E157", {"start": v(-24.43, -14.51) * mm, "end": v(-24.48, -14.46) * mm});
            skLineSegment(sketch, "E158", {"start": v(-24.48, -14.46) * mm, "end": v(-24.54, -14.4) * mm});
            skLineSegment(sketch, "E159", {"start": v(-24.54, -14.4) * mm, "end": v(-24.59, -14.35) * mm});
            skLineSegment(sketch, "E160", {"start": v(-24.59, -14.35) * mm, "end": v(-24.63, -14.3) * mm});
            skLineSegment(sketch, "E161", {"start": v(-24.63, -14.3) * mm, "end": v(-24.68, -14.23) * mm});
            skLineSegment(sketch, "E162", {"start": v(-24.68, -14.23) * mm, "end": v(-24.72, -14.17) * mm});
            skLineSegment(sketch, "E163", {"start": v(-24.72, -14.17) * mm, "end": v(-24.76, -14.1) * mm});
            skLineSegment(sketch, "E164", {"start": v(-24.76, -14.1) * mm, "end": v(-24.8, -14.04) * mm});
            skLineSegment(sketch, "E165", {"start": v(-24.8, -14.04) * mm, "end": v(-24.82, -13.97) * mm});
            skLineSegment(sketch, "E166", {"start": v(-24.82, -13.97) * mm, "end": v(-24.85, -13.9) * mm});
            skLineSegment(sketch, "E167", {"start": v(-24.85, -13.9) * mm, "end": v(-24.88, -13.83) * mm});
            skLineSegment(sketch, "E168", {"start": v(-24.88, -13.83) * mm, "end": v(-24.9, -13.76) * mm});
            skLineSegment(sketch, "E169", {"start": v(-24.9, -13.76) * mm, "end": v(-24.92, -13.66) * mm});
            skLineSegment(sketch, "E170", {"start": v(-24.92, -13.66) * mm, "end": v(-24.94, -13.55) * mm});
            skLineSegment(sketch, "E171", {"start": v(-24.94, -13.55) * mm, "end": v(-24.96, -13.38) * mm});
            skLineSegment(sketch, "E172", {"start": v(-24.96, -13.38) * mm, "end": v(-24.98, -12.8) * mm});
            skLineSegment(sketch, "E173", {"start": v(-24.98, -12.8) * mm, "end": v(-24.98, -3.92) * mm});
            skLineSegment(sketch, "E174", {"start": v(-24.98, -3.92) * mm, "end": v(-24.97, -3.38) * mm});
            skLineSegment(sketch, "E175", {"start": v(-24.97, -3.38) * mm, "end": v(-24.96, -3.24) * mm});
            skLineSegment(sketch, "E176", {"start": v(-24.96, -3.24) * mm, "end": v(-24.95, -3.15) * mm});
            skLineSegment(sketch, "E177", {"start": v(-24.95, -3.15) * mm, "end": v(-24.94, -3.1) * mm});
            skLineSegment(sketch, "E178", {"start": v(-24.94, -3.1) * mm, "end": v(-24.93, -3.06) * mm});
            skLineSegment(sketch, "E179", {"start": v(-24.93, -3.06) * mm, "end": v(-24.93, -3.02) * mm});
            skLineSegment(sketch, "E180", {"start": v(-24.93, -3.02) * mm, "end": v(-24.92, -2.97) * mm});
            skLineSegment(sketch, "E181", {"start": v(-24.92, -2.97) * mm, "end": v(-24.9, -2.93) * mm});
            skLineSegment(sketch, "E182", {"start": v(-24.9, -2.93) * mm, "end": v(-24.9, -2.88) * mm});
            skLineSegment(sketch, "E183", {"start": v(-24.9, -2.88) * mm, "end": v(-24.88, -2.84) * mm});
            skLineSegment(sketch, "E184", {"start": v(-24.88, -2.84) * mm, "end": v(-24.87, -2.8) * mm});
            skLineSegment(sketch, "E185", {"start": v(-24.87, -2.8) * mm, "end": v(-24.85, -2.76) * mm});
            skLineSegment(sketch, "E186", {"start": v(-24.85, -2.76) * mm, "end": v(-24.83, -2.71) * mm});
            skLineSegment(sketch, "E187", {"start": v(-24.83, -2.71) * mm, "end": v(-24.81, -2.67) * mm});
            skLineSegment(sketch, "E188", {"start": v(-24.81, -2.67) * mm, "end": v(-24.8, -2.63) * mm});
            skLineSegment(sketch, "E189", {"start": v(-24.8, -2.63) * mm, "end": v(-24.77, -2.58) * mm});
            skLineSegment(sketch, "E190", {"start": v(-24.77, -2.58) * mm, "end": v(-24.74, -2.53) * mm});
            skLineSegment(sketch, "E191", {"start": v(-24.74, -2.53) * mm, "end": v(-24.7, -2.48) * mm});
            skLineSegment(sketch, "E192", {"start": v(-24.7, -2.48) * mm, "end": v(-24.68, -2.43) * mm});
            skLineSegment(sketch, "E193", {"start": v(-24.68, -2.43) * mm, "end": v(-24.64, -2.38) * mm});
            skLineSegment(sketch, "E194", {"start": v(-24.64, -2.38) * mm, "end": v(-24.6, -2.34) * mm});
            skLineSegment(sketch, "E195", {"start": v(-24.6, -2.34) * mm, "end": v(-24.57, -2.3) * mm});
            skLineSegment(sketch, "E196", {"start": v(-24.57, -2.3) * mm, "end": v(-24.53, -2.25) * mm});
            skLineSegment(sketch, "E197", {"start": v(-24.53, -2.25) * mm, "end": v(-24.5, -2.2) * mm});
            skLineSegment(sketch, "E198", {"start": v(-24.5, -2.2) * mm, "end": v(-24.45, -2.16) * mm});
            skLineSegment(sketch, "E199", {"start": v(-24.45, -2.16) * mm, "end": v(-24.41, -2.12) * mm});
            skLineSegment(sketch, "E200", {"start": v(-24.41, -2.12) * mm, "end": v(-24.37, -2.08) * mm});
            skLineSegment(sketch, "E201", {"start": v(-24.37, -2.08) * mm, "end": v(-24.32, -2.05) * mm});
            skLineSegment(sketch, "E202", {"start": v(-24.32, -2.05) * mm, "end": v(-24.28, -2.01) * mm});
            skLineSegment(sketch, "E203", {"start": v(-24.28, -2.01) * mm, "end": v(-24.23, -1.98) * mm});
            skLineSegment(sketch, "E204", {"start": v(-24.23, -1.98) * mm, "end": v(-24.18, -1.94) * mm});
            skLineSegment(sketch, "E205", {"start": v(-24.18, -1.94) * mm, "end": v(-24.13, -1.91) * mm});
            skLineSegment(sketch, "E206", {"start": v(-24.13, -1.91) * mm, "end": v(-24.08, -1.88) * mm});
            skLineSegment(sketch, "E207", {"start": v(-24.08, -1.88) * mm, "end": v(-24.03, -1.86) * mm});
            skLineSegment(sketch, "E208", {"start": v(-24.03, -1.86) * mm, "end": v(-23.98, -1.83) * mm});
            skLineSegment(sketch, "E209", {"start": v(-23.98, -1.83) * mm, "end": v(-23.93, -1.8) * mm});
            skLineSegment(sketch, "E210", {"start": v(-23.93, -1.8) * mm, "end": v(-23.87, -1.79) * mm});
            skLineSegment(sketch, "E211", {"start": v(-23.87, -1.79) * mm, "end": v(-23.82, -1.77) * mm});
            skLineSegment(sketch, "E212", {"start": v(-23.82, -1.77) * mm, "end": v(-23.76, -1.75) * mm});
            skLineSegment(sketch, "E213", {"start": v(-23.76, -1.75) * mm, "end": v(-23.7, -1.73) * mm});
            skLineSegment(sketch, "E214", {"start": v(-23.7, -1.73) * mm, "end": v(-23.65, -1.72) * mm});
            skLineSegment(sketch, "E215", {"start": v(-23.65, -1.72) * mm, "end": v(-23.6, -1.71) * mm});
            skLineSegment(sketch, "E216", {"start": v(-23.6, -1.71) * mm, "end": v(-23.53, -1.7) * mm});
            skLineSegment(sketch, "E217", {"start": v(-23.53, -1.7) * mm, "end": v(-23.48, -1.7) * mm});
            skLineSegment(sketch, "E218", {"start": v(-23.48, -1.7) * mm, "end": v(-23.32, -1.69) * mm});
            skLineSegment(sketch, "E219", {"start": v(-23.32, -1.69) * mm, "end": v(-23.17, -1.68) * mm});
            skLineSegment(sketch, "E220", {"start": v(-23.17, -1.68) * mm, "end": v(-22.95, -1.67) * mm});
            skLineSegment(sketch, "E221", {"start": v(-22.95, -1.67) * mm, "end": v(-21.9, -1.67) * mm});
            skLineSegment(sketch, "E222", {"start": v(-21.9, -1.67) * mm, "end": v(-21.52, -1.67) * mm});
            skLineSegment(sketch, "E223", {"start": v(-21.52, -1.67) * mm, "end": v(-21.3, -1.66) * mm});
            skLineSegment(sketch, "E224", {"start": v(-21.3, -1.66) * mm, "end": v(-21.2, -1.64) * mm});
            skLineSegment(sketch, "E225", {"start": v(-21.2, -1.64) * mm, "end": v(-20.86, -1.5) * mm});
            skLineSegment(sketch, "E226", {"start": v(-20.86, -1.5) * mm, "end": v(-17.7, 0.02) * mm});
            skLineSegment(sketch, "E227", {"start": v(-17.7, 0.02) * mm, "end": v(-17.01, 0.36) * mm});
            skLineSegment(sketch, "E228", {"start": v(-15.75, 0.24) * mm, "end": v(-14.06, -0.59) * mm});
            skLineSegment(sketch, "E229", {"start": v(-14.06, -0.59) * mm, "end": v(-14.06, 0.58) * mm});
            skLineSegment(sketch, "E230", {"start": v(-13.15, -0.33) * mm, "end": v(-13.15, -2.1) * mm});
            skLineSegment(sketch, "E231", {"start": v(-13.15, -2.1) * mm, "end": v(-13.26, -2.06) * mm});
            skLineSegment(sketch, "E232", {"start": v(-13.26, -2.06) * mm, "end": v(-13.9, -1.75) * mm});
            skLineSegment(sketch, "E233", {"start": v(-16.83, -0.6) * mm, "end": v(-17.05, -0.71) * mm});
            skLineSegment(sketch, "E234", {"start": v(-17.05, -0.71) * mm, "end": v(-17.27, -0.83) * mm});
            skLineSegment(sketch, "E235", {"start": v(-17.27, -0.83) * mm, "end": v(-18.4, -1.4) * mm});
            skLineSegment(sketch, "E236", {"start": v(-18.4, -1.4) * mm, "end": v(-22.7, -3.51) * mm});
            skLineSegment(sketch, "E237", {"start": v(-22.7, -3.51) * mm, "end": v(-23.6, -3.97) * mm});
            skLineSegment(sketch, "E238", {"start": v(-23.6, -3.97) * mm, "end": v(-23.64, -4) * mm});
            skLineSegment(sketch, "E239", {"start": v(-23.64, -4) * mm, "end": v(-23.69, -4.02) * mm});
            skLineSegment(sketch, "E240", {"start": v(-23.69, -4.02) * mm, "end": v(-23.73, -4.05) * mm});
            skLineSegment(sketch, "E241", {"start": v(-23.73, -4.05) * mm, "end": v(-23.76, -4.08) * mm});
            skLineSegment(sketch, "E242", {"start": v(-23.76, -4.08) * mm, "end": v(-23.79, -4.1) * mm});
            skLineSegment(sketch, "E243", {"start": v(-23.79, -4.1) * mm, "end": v(-23.8, -4.13) * mm});
            skLineSegment(sketch, "E244", {"start": v(-23.8, -4.13) * mm, "end": v(-23.82, -4.15) * mm});
            skLineSegment(sketch, "E245", {"start": v(-23.82, -4.15) * mm, "end": v(-23.83, -4.16) * mm});
            skLineSegment(sketch, "E246", {"start": v(-23.83, -4.16) * mm, "end": v(-23.83, -4.18) * mm});
            skLineSegment(sketch, "E247", {"start": v(-23.83, -4.18) * mm, "end": v(-23.84, -4.2) * mm});
            skLineSegment(sketch, "E248", {"start": v(-23.84, -4.2) * mm, "end": v(-23.85, -4.21) * mm});
            skLineSegment(sketch, "E249", {"start": v(-23.85, -4.21) * mm, "end": v(-23.85, -4.23) * mm});
            skLineSegment(sketch, "E250", {"start": v(-23.85, -4.23) * mm, "end": v(-23.85, -4.25) * mm});
            skLineSegment(sketch, "E251", {"start": v(-23.85, -4.25) * mm, "end": v(-23.86, -4.27) * mm});
            skLineSegment(sketch, "E252", {"start": v(-23.86, -4.27) * mm, "end": v(-23.86, -4.29) * mm});
            skLineSegment(sketch, "E253", {"start": v(-23.86, -4.29) * mm, "end": v(-23.86, -4.3) * mm});
            skLineSegment(sketch, "E254", {"start": v(-23.86, -4.3) * mm, "end": v(-23.85, -4.32) * mm});
            skLineSegment(sketch, "E255", {"start": v(-23.85, -4.32) * mm, "end": v(-23.85, -4.34) * mm});
            skLineSegment(sketch, "E256", {"start": v(-23.85, -4.34) * mm, "end": v(-23.84, -4.36) * mm});
            skLineSegment(sketch, "E257", {"start": v(-23.84, -4.36) * mm, "end": v(-23.84, -4.38) * mm});
            skLineSegment(sketch, "E258", {"start": v(-23.84, -4.38) * mm, "end": v(-23.83, -4.4) * mm});
            skLineSegment(sketch, "E259", {"start": v(-23.83, -4.4) * mm, "end": v(-23.82, -4.42) * mm});
            skLineSegment(sketch, "E260", {"start": v(-23.82, -4.42) * mm, "end": v(-23.81, -4.44) * mm});
            skLineSegment(sketch, "E261", {"start": v(-23.81, -4.44) * mm, "end": v(-23.8, -4.45) * mm});
            skLineSegment(sketch, "E262", {"start": v(-23.8, -4.45) * mm, "end": v(-23.8, -4.47) * mm});
            skLineSegment(sketch, "E263", {"start": v(-23.8, -4.47) * mm, "end": v(-23.78, -4.48) * mm});
            skLineSegment(sketch, "E264", {"start": v(-23.78, -4.48) * mm, "end": v(-23.76, -4.5) * mm});
            skLineSegment(sketch, "E265", {"start": v(-23.76, -4.5) * mm, "end": v(-23.73, -4.53) * mm});
            skLineSegment(sketch, "E266", {"start": v(-23.73, -4.53) * mm, "end": v(-23.7, -4.55) * mm});
            skLineSegment(sketch, "E267", {"start": v(-23.7, -4.55) * mm, "end": v(-23.58, -4.62) * mm});
            skLineSegment(sketch, "E268", {"start": v(-23.58, -4.62) * mm, "end": v(-23.42, -4.7) * mm});
            skLineSegment(sketch, "E269", {"start": v(-23.42, -4.7) * mm, "end": v(-19.6, -6.6) * mm});
            skLineSegment(sketch, "E270", {"start": v(-19.6, -6.6) * mm, "end": v(-18.6, -7.09) * mm});
            skLineSegment(sketch, "E271", {"start": v(-18.6, -7.09) * mm, "end": v(-17.5, -7.65) * mm});
            skLineSegment(sketch, "E272", {"start": v(-17.5, -7.65) * mm, "end": v(-16.7, -8.03) * mm});
            skLineSegment(sketch, "E273", {"start": v(-16.7, -8.03) * mm, "end": v(-16.68, -8.04) * mm});
            skLineSegment(sketch, "E274", {"start": v(-16.68, -8.04) * mm, "end": v(-16.66, -8.05) * mm});
            skLineSegment(sketch, "E275", {"start": v(-16.66, -8.05) * mm, "end": v(-16.64, -8.06) * mm});
            skLineSegment(sketch, "E276", {"start": v(-16.64, -8.06) * mm, "end": v(-16.62, -8.06) * mm});
            skLineSegment(sketch, "E277", {"start": v(-16.62, -8.06) * mm, "end": v(-16.6, -8.07) * mm});
            skLineSegment(sketch, "E278", {"start": v(-16.6, -8.07) * mm, "end": v(-16.58, -8.07) * mm});
            skLineSegment(sketch, "E279", {"start": v(-16.58, -8.07) * mm, "end": v(-16.56, -8.07) * mm});
            skLineSegment(sketch, "E280", {"start": v(-16.56, -8.07) * mm, "end": v(-16.54, -8.07) * mm});
            skLineSegment(sketch, "E281", {"start": v(-16.54, -8.07) * mm, "end": v(-16.52, -8.08) * mm});
            skLineSegment(sketch, "E282", {"start": v(-16.52, -8.08) * mm, "end": v(-16.48, -8.07) * mm});
            skLineSegment(sketch, "E283", {"start": v(-16.48, -8.07) * mm, "end": v(-16.44, -8.07) * mm});
            skLineSegment(sketch, "E284", {"start": v(-16.44, -8.07) * mm, "end": v(-16.4, -8.06) * mm});
            skLineSegment(sketch, "E285", {"start": v(-16.4, -8.06) * mm, "end": v(-16.32, -8.04) * mm});
            skLineSegment(sketch, "E286", {"start": v(-16.32, -8.04) * mm, "end": v(-16.14, -7.96) * mm});
            skLineSegment(sketch, "E287", {"start": v(-16.14, -7.96) * mm, "end": v(-13.76, -6.78) * mm});
            skLineSegment(sketch, "E288", {"start": v(-13.76, -6.78) * mm, "end": v(-9.85, -4.84) * mm});
            skLineSegment(sketch, "E289", {"start": v(-9.4, -3.99) * mm, "end": v(-9.57, -3.89) * mm});
            skLineSegment(sketch, "E290", {"start": v(-9.57, -3.89) * mm, "end": v(-10.59, -3.4) * mm});
            skLineSegment(sketch, "E291", {"start": v(-10.59, -3.4) * mm, "end": v(-10.6, -0.33) * mm});
            skLineSegment(sketch, "E292", {"start": v(-10.6, -0.33) * mm, "end": v(-13.15, -0.33) * mm});
            skLineSegment(sketch, "E293", {"start": v(-26.34, -4.98) * mm, "end": v(-25.3, -4.97) * mm});
            skLineSegment(sketch, "E294", {"start": v(-25.3, -4.97) * mm, "end": v(-25.28, -6.53) * mm});
            skLineSegment(sketch, "E295", {"start": v(-25.28, -6.53) * mm, "end": v(-26.11, -6.52) * mm});
            skLineSegment(sketch, "E296", {"start": v(-26.11, -6.52) * mm, "end": v(-26.27, -6.5) * mm});
            skLineSegment(sketch, "E297", {"start": v(-26.27, -6.5) * mm, "end": v(-26.38, -6.49) * mm});
            skLineSegment(sketch, "E298", {"start": v(-26.38, -6.49) * mm, "end": v(-26.4, -6.47) * mm});
            skLineSegment(sketch, "E299", {"start": v(-26.4, -6.47) * mm, "end": v(-26.43, -6.45) * mm});
            skLineSegment(sketch, "E300", {"start": v(-26.43, -6.45) * mm, "end": v(-26.45, -6.43) * mm});
            skLineSegment(sketch, "E301", {"start": v(-26.45, -6.43) * mm, "end": v(-26.47, -6.41) * mm});
            skLineSegment(sketch, "E302", {"start": v(-26.47, -6.41) * mm, "end": v(-26.49, -6.39) * mm});
            skLineSegment(sketch, "E303", {"start": v(-26.49, -6.39) * mm, "end": v(-26.5, -6.37) * mm});
            skLineSegment(sketch, "E304", {"start": v(-26.5, -6.37) * mm, "end": v(-26.52, -6.34) * mm});
            skLineSegment(sketch, "E305", {"start": v(-26.52, -6.34) * mm, "end": v(-26.54, -6.32) * mm});
            skLineSegment(sketch, "E306", {"start": v(-26.54, -6.32) * mm, "end": v(-26.55, -6.29) * mm});
            skLineSegment(sketch, "E307", {"start": v(-26.55, -6.29) * mm, "end": v(-26.56, -6.26) * mm});
            skLineSegment(sketch, "E308", {"start": v(-26.56, -6.26) * mm, "end": v(-26.57, -6.23) * mm});
            skLineSegment(sketch, "E309", {"start": v(-26.57, -6.23) * mm, "end": v(-26.58, -6.2) * mm});
            skLineSegment(sketch, "E310", {"start": v(-26.58, -6.2) * mm, "end": v(-26.59, -6.18) * mm});
            skLineSegment(sketch, "E311", {"start": v(-26.59, -6.18) * mm, "end": v(-26.6, -6.15) * mm});
            skLineSegment(sketch, "E312", {"start": v(-26.6, -6.15) * mm, "end": v(-26.6, -6.09) * mm});
            skLineSegment(sketch, "E313", {"start": v(-26.6, -6.09) * mm, "end": v(-26.62, -6.03) * mm});
            skLineSegment(sketch, "E314", {"start": v(-26.62, -6.03) * mm, "end": v(-26.62, -5.9) * mm});
            skLineSegment(sketch, "E315", {"start": v(-26.62, -5.9) * mm, "end": v(-26.63, -5.75) * mm});
            skLineSegment(sketch, "E316", {"start": v(-26.63, -5.75) * mm, "end": v(-26.63, -5.7) * mm});
            skLineSegment(sketch, "E317", {"start": v(-26.63, -5.7) * mm, "end": v(-26.63, -5.62) * mm});
            skLineSegment(sketch, "E318", {"start": v(-26.63, -5.62) * mm, "end": v(-26.62, -5.5) * mm});
            skLineSegment(sketch, "E319", {"start": v(-26.62, -5.5) * mm, "end": v(-26.6, -5.42) * mm});
            skLineSegment(sketch, "E320", {"start": v(-26.6, -5.42) * mm, "end": v(-26.6, -5.36) * mm});
            skLineSegment(sketch, "E321", {"start": v(-26.6, -5.36) * mm, "end": v(-26.58, -5.3) * mm});
            skLineSegment(sketch, "E322", {"start": v(-26.58, -5.3) * mm, "end": v(-26.58, -5.28) * mm});
            skLineSegment(sketch, "E323", {"start": v(-26.58, -5.28) * mm, "end": v(-26.57, -5.25) * mm});
            skLineSegment(sketch, "E324", {"start": v(-26.57, -5.25) * mm, "end": v(-26.56, -5.23) * mm});
            skLineSegment(sketch, "E325", {"start": v(-26.56, -5.23) * mm, "end": v(-26.55, -5.2) * mm});
            skLineSegment(sketch, "E326", {"start": v(-26.55, -5.2) * mm, "end": v(-26.53, -5.18) * mm});
            skLineSegment(sketch, "E327", {"start": v(-26.53, -5.18) * mm, "end": v(-26.52, -5.15) * mm});
            skLineSegment(sketch, "E328", {"start": v(-26.52, -5.15) * mm, "end": v(-26.5, -5.13) * mm});
            skLineSegment(sketch, "E329", {"start": v(-26.5, -5.13) * mm, "end": v(-26.5, -5.1) * mm});
            skLineSegment(sketch, "E330", {"start": v(-26.5, -5.1) * mm, "end": v(-26.47, -5.09) * mm});
            skLineSegment(sketch, "E331", {"start": v(-26.47, -5.09) * mm, "end": v(-26.46, -5.07) * mm});
            skLineSegment(sketch, "E332", {"start": v(-26.46, -5.07) * mm, "end": v(-26.44, -5.05) * mm});
            skLineSegment(sketch, "E333", {"start": v(-26.44, -5.05) * mm, "end": v(-26.42, -5.03) * mm});
            skLineSegment(sketch, "E334", {"start": v(-26.42, -5.03) * mm, "end": v(-26.4, -5.01) * mm});
            skLineSegment(sketch, "E335", {"start": v(-26.4, -5.01) * mm, "end": v(-26.37, -5) * mm});
            skLineSegment(sketch, "E336", {"start": v(-26.37, -5) * mm, "end": v(-26.34, -4.98) * mm});
            skLineSegment(sketch, "E337", {"start": v(-7.72, -4.97) * mm, "end": v(-7.68, -4.98) * mm});
            skLineSegment(sketch, "E338", {"start": v(-7.68, -4.98) * mm, "end": v(-7.64, -4.98) * mm});
            skLineSegment(sketch, "E339", {"start": v(-7.64, -4.98) * mm, "end": v(-7.6, -4.98) * mm});
            skLineSegment(sketch, "E340", {"start": v(-7.6, -4.98) * mm, "end": v(-7.55, -4.98) * mm});
            skLineSegment(sketch, "E341", {"start": v(-7.55, -4.98) * mm, "end": v(-7.5, -4.98) * mm});
            skLineSegment(sketch, "E342", {"start": v(-7.5, -4.98) * mm, "end": v(-7.41, -4.97) * mm});
            skLineSegment(sketch, "E343", {"start": v(-7.41, -4.97) * mm, "end": v(-7.13, -4.95) * mm});
            skLineSegment(sketch, "E344", {"start": v(-7.13, -4.95) * mm, "end": v(-7.09, -4.94) * mm});
            skLineSegment(sketch, "E345", {"start": v(-7.09, -4.94) * mm, "end": v(-7.04, -4.94) * mm});
            skLineSegment(sketch, "E346", {"start": v(-7.04, -4.94) * mm, "end": v(-7, -4.94) * mm});
            skLineSegment(sketch, "E347", {"start": v(-7, -4.94) * mm, "end": v(-6.95, -4.94) * mm});
            skLineSegment(sketch, "E348", {"start": v(-6.95, -4.94) * mm, "end": v(-6.9, -4.94) * mm});
            skLineSegment(sketch, "E349", {"start": v(-6.9, -4.94) * mm, "end": v(-6.86, -4.95) * mm});
            skLineSegment(sketch, "E350", {"start": v(-6.86, -4.95) * mm, "end": v(-6.82, -4.95) * mm});
            skLineSegment(sketch, "E351", {"start": v(-6.82, -4.95) * mm, "end": v(-6.78, -4.96) * mm});
            skLineSegment(sketch, "E352", {"start": v(-6.78, -4.96) * mm, "end": v(-6.74, -4.97) * mm});
            skLineSegment(sketch, "E353", {"start": v(-6.74, -4.97) * mm, "end": v(-6.7, -4.99) * mm});
            skLineSegment(sketch, "E354", {"start": v(-6.7, -4.99) * mm, "end": v(-6.66, -5) * mm});
            skLineSegment(sketch, "E355", {"start": v(-6.66, -5) * mm, "end": v(-6.62, -5.03) * mm});
            skLineSegment(sketch, "E356", {"start": v(-6.62, -5.03) * mm, "end": v(-6.58, -5.05) * mm});
            skLineSegment(sketch, "E357", {"start": v(-6.58, -5.05) * mm, "end": v(-6.55, -5.08) * mm});
            skLineSegment(sketch, "E358", {"start": v(-6.55, -5.08) * mm, "end": v(-6.52, -5.1) * mm});
            skLineSegment(sketch, "E359", {"start": v(-6.52, -5.1) * mm, "end": v(-6.48, -5.14) * mm});
            skLineSegment(sketch, "E360", {"start": v(-6.48, -5.14) * mm, "end": v(-6.47, -5.18) * mm});
            skLineSegment(sketch, "E361", {"start": v(-6.47, -5.18) * mm, "end": v(-6.46, -5.21) * mm});
            skLineSegment(sketch, "E362", {"start": v(-6.46, -5.21) * mm, "end": v(-6.45, -5.24) * mm});
            skLineSegment(sketch, "E363", {"start": v(-6.45, -5.24) * mm, "end": v(-6.43, -5.31) * mm});
            skLineSegment(sketch, "E364", {"start": v(-6.43, -5.31) * mm, "end": v(-6.41, -5.38) * mm});
            skLineSegment(sketch, "E365", {"start": v(-6.41, -5.38) * mm, "end": v(-6.4, -5.45) * mm});
            skLineSegment(sketch, "E366", {"start": v(-6.4, -5.45) * mm, "end": v(-6.4, -5.52) * mm});
            skLineSegment(sketch, "E367", {"start": v(-6.4, -5.52) * mm, "end": v(-6.39, -5.59) * mm});
            skLineSegment(sketch, "E368", {"start": v(-6.39, -5.59) * mm, "end": v(-6.38, -5.7) * mm});
            skLineSegment(sketch, "E369", {"start": v(-6.38, -5.7) * mm, "end": v(-6.39, -5.83) * mm});
            skLineSegment(sketch, "E370", {"start": v(-6.39, -5.83) * mm, "end": v(-6.4, -6.08) * mm});
            skLineSegment(sketch, "E371", {"start": v(-6.4, -6.08) * mm, "end": v(-6.42, -6.15) * mm});
            skLineSegment(sketch, "E372", {"start": v(-6.42, -6.15) * mm, "end": v(-6.47, -6.3) * mm});
            skLineSegment(sketch, "E373", {"start": v(-6.47, -6.3) * mm, "end": v(-6.5, -6.36) * mm});
            skLineSegment(sketch, "E374", {"start": v(-6.5, -6.36) * mm, "end": v(-6.53, -6.4) * mm});
            skLineSegment(sketch, "E375", {"start": v(-6.53, -6.4) * mm, "end": v(-6.56, -6.43) * mm});
            skLineSegment(sketch, "E376", {"start": v(-6.56, -6.43) * mm, "end": v(-6.59, -6.46) * mm});
            skLineSegment(sketch, "E377", {"start": v(-6.59, -6.46) * mm, "end": v(-6.61, -6.47) * mm});
            skLineSegment(sketch, "E378", {"start": v(-6.61, -6.47) * mm, "end": v(-6.64, -6.49) * mm});
            skLineSegment(sketch, "E379", {"start": v(-6.64, -6.49) * mm, "end": v(-6.67, -6.5) * mm});
            skLineSegment(sketch, "E380", {"start": v(-6.67, -6.5) * mm, "end": v(-7.74, -6.53) * mm});
            skLineSegment(sketch, "E381", {"start": v(-7.74, -6.53) * mm, "end": v(-7.72, -4.97) * mm});
            skLineSegment(sketch, "E382", {"start": v(-26.35, -7.32) * mm, "end": v(-25.28, -7.3) * mm});
            skLineSegment(sketch, "E383", {"start": v(-25.28, -7.3) * mm, "end": v(-25.28, -8.87) * mm});
            skLineSegment(sketch, "E384", {"start": v(-25.28, -8.87) * mm, "end": v(-26.35, -8.85) * mm});
            skLineSegment(sketch, "E385", {"start": v(-26.35, -8.85) * mm, "end": v(-26.5, -8.7) * mm});
            skLineSegment(sketch, "E386", {"start": v(-26.5, -8.7) * mm, "end": v(-26.55, -8.62) * mm});
            skLineSegment(sketch, "E387", {"start": v(-26.55, -8.62) * mm, "end": v(-26.57, -8.57) * mm});
            skLineSegment(sketch, "E388", {"start": v(-26.57, -8.57) * mm, "end": v(-26.6, -8.52) * mm});
            skLineSegment(sketch, "E389", {"start": v(-26.6, -8.52) * mm, "end": v(-26.6, -8.47) * mm});
            skLineSegment(sketch, "E390", {"start": v(-26.6, -8.47) * mm, "end": v(-26.6, -8.45) * mm});
            skLineSegment(sketch, "E391", {"start": v(-26.6, -8.45) * mm, "end": v(-26.61, -8.37) * mm});
            skLineSegment(sketch, "E392", {"start": v(-26.61, -8.37) * mm, "end": v(-26.63, -8.2) * mm});
            skLineSegment(sketch, "E393", {"start": v(-26.63, -8.2) * mm, "end": v(-26.63, -8.08) * mm});
            skLineSegment(sketch, "E394", {"start": v(-26.63, -8.08) * mm, "end": v(-26.64, -8) * mm});
            skLineSegment(sketch, "E395", {"start": v(-26.64, -8) * mm, "end": v(-26.64, -7.95) * mm});
            skLineSegment(sketch, "E396", {"start": v(-26.64, -7.95) * mm, "end": v(-26.63, -7.9) * mm});
            skLineSegment(sketch, "E397", {"start": v(-26.63, -7.9) * mm, "end": v(-26.63, -7.86) * mm});
            skLineSegment(sketch, "E398", {"start": v(-26.63, -7.86) * mm, "end": v(-26.63, -7.82) * mm});
            skLineSegment(sketch, "E399", {"start": v(-26.63, -7.82) * mm, "end": v(-26.62, -7.78) * mm});
            skLineSegment(sketch, "E400", {"start": v(-26.62, -7.78) * mm, "end": v(-26.61, -7.74) * mm});
            skLineSegment(sketch, "E401", {"start": v(-26.61, -7.74) * mm, "end": v(-26.6, -7.7) * mm});
            skLineSegment(sketch, "E402", {"start": v(-26.6, -7.7) * mm, "end": v(-26.6, -7.66) * mm});
            skLineSegment(sketch, "E403", {"start": v(-26.6, -7.66) * mm, "end": v(-26.58, -7.62) * mm});
            skLineSegment(sketch, "E404", {"start": v(-26.58, -7.62) * mm, "end": v(-26.56, -7.58) * mm});
            skLineSegment(sketch, "E405", {"start": v(-26.56, -7.58) * mm, "end": v(-26.55, -7.54) * mm});
            skLineSegment(sketch, "E406", {"start": v(-26.55, -7.54) * mm, "end": v(-26.53, -7.5) * mm});
            skLineSegment(sketch, "E407", {"start": v(-26.53, -7.5) * mm, "end": v(-26.5, -7.47) * mm});
            skLineSegment(sketch, "E408", {"start": v(-26.5, -7.47) * mm, "end": v(-26.48, -7.44) * mm});
            skLineSegment(sketch, "E409", {"start": v(-26.48, -7.44) * mm, "end": v(-26.45, -7.4) * mm});
            skLineSegment(sketch, "E410", {"start": v(-26.45, -7.4) * mm, "end": v(-26.42, -7.38) * mm});
            skLineSegment(sketch, "E411", {"start": v(-26.42, -7.38) * mm, "end": v(-26.39, -7.35) * mm});
            skLineSegment(sketch, "E412", {"start": v(-26.39, -7.35) * mm, "end": v(-26.35, -7.32) * mm});
            skLineSegment(sketch, "E413", {"start": v(-7.73, -7.3) * mm, "end": v(-6.66, -7.32) * mm});
            skLineSegment(sketch, "E414", {"start": v(-6.66, -7.32) * mm, "end": v(-6.53, -7.44) * mm});
            skLineSegment(sketch, "E415", {"start": v(-6.53, -7.44) * mm, "end": v(-6.47, -7.53) * mm});
            skLineSegment(sketch, "E416", {"start": v(-6.47, -7.53) * mm, "end": v(-6.44, -7.58) * mm});
            skLineSegment(sketch, "E417", {"start": v(-6.44, -7.58) * mm, "end": v(-6.43, -7.63) * mm});
            skLineSegment(sketch, "E418", {"start": v(-6.43, -7.63) * mm, "end": v(-6.41, -7.68) * mm});
            skLineSegment(sketch, "E419", {"start": v(-6.41, -7.68) * mm, "end": v(-6.4, -7.7) * mm});
            skLineSegment(sketch, "E420", {"start": v(-6.4, -7.7) * mm, "end": v(-6.4, -7.79) * mm});
            skLineSegment(sketch, "E421", {"start": v(-6.4, -7.79) * mm, "end": v(-6.39, -7.96) * mm});
            skLineSegment(sketch, "E422", {"start": v(-6.39, -7.96) * mm, "end": v(-6.38, -8.09) * mm});
            skLineSegment(sketch, "E423", {"start": v(-6.38, -8.09) * mm, "end": v(-6.38, -8.17) * mm});
            skLineSegment(sketch, "E424", {"start": v(-6.38, -8.17) * mm, "end": v(-6.38, -8.22) * mm});
            skLineSegment(sketch, "E425", {"start": v(-6.38, -8.22) * mm, "end": v(-6.38, -8.26) * mm});
            skLineSegment(sketch, "E426", {"start": v(-6.38, -8.26) * mm, "end": v(-6.38, -8.3) * mm});
            skLineSegment(sketch, "E427", {"start": v(-6.38, -8.3) * mm, "end": v(-6.39, -8.34) * mm});
            skLineSegment(sketch, "E428", {"start": v(-6.39, -8.34) * mm, "end": v(-6.4, -8.39) * mm});
            skLineSegment(sketch, "E429", {"start": v(-6.4, -8.39) * mm, "end": v(-6.4, -8.43) * mm});
            skLineSegment(sketch, "E430", {"start": v(-6.4, -8.43) * mm, "end": v(-6.4, -8.47) * mm});
            skLineSegment(sketch, "E431", {"start": v(-6.4, -8.47) * mm, "end": v(-6.42, -8.5) * mm});
            skLineSegment(sketch, "E432", {"start": v(-6.42, -8.5) * mm, "end": v(-6.43, -8.55) * mm});
            skLineSegment(sketch, "E433", {"start": v(-6.43, -8.55) * mm, "end": v(-6.45, -8.58) * mm});
            skLineSegment(sketch, "E434", {"start": v(-6.45, -8.58) * mm, "end": v(-6.47, -8.62) * mm});
            skLineSegment(sketch, "E435", {"start": v(-6.47, -8.62) * mm, "end": v(-6.49, -8.66) * mm});
            skLineSegment(sketch, "E436", {"start": v(-6.49, -8.66) * mm, "end": v(-6.5, -8.7) * mm});
            skLineSegment(sketch, "E437", {"start": v(-6.5, -8.7) * mm, "end": v(-6.53, -8.73) * mm});
            skLineSegment(sketch, "E438", {"start": v(-6.53, -8.73) * mm, "end": v(-6.56, -8.76) * mm});
            skLineSegment(sketch, "E439", {"start": v(-6.56, -8.76) * mm, "end": v(-6.6, -8.79) * mm});
            skLineSegment(sketch, "E440", {"start": v(-6.6, -8.79) * mm, "end": v(-6.62, -8.82) * mm});
            skLineSegment(sketch, "E441", {"start": v(-6.62, -8.82) * mm, "end": v(-6.66, -8.85) * mm});
            skLineSegment(sketch, "E442", {"start": v(-6.66, -8.85) * mm, "end": v(-7.73, -8.87) * mm});
            skLineSegment(sketch, "E443", {"start": v(-7.73, -8.87) * mm, "end": v(-7.73, -7.3) * mm});
            skLineSegment(sketch, "E444", {"start": v(-26.38, -9.67) * mm, "end": v(-26.27, -9.66) * mm});
            skLineSegment(sketch, "E445", {"start": v(-26.27, -9.66) * mm, "end": v(-26.08, -9.64) * mm});
            skLineSegment(sketch, "E446", {"start": v(-26.08, -9.64) * mm, "end": v(-25.28, -9.63) * mm});
            skLineSegment(sketch, "E447", {"start": v(-25.28, -9.63) * mm, "end": v(-25.3, -11.2) * mm});
            skLineSegment(sketch, "E448", {"start": v(-25.3, -11.2) * mm, "end": v(-26.03, -11.2) * mm});
            skLineSegment(sketch, "E449", {"start": v(-26.03, -11.2) * mm, "end": v(-26.17, -11.2) * mm});
            skLineSegment(sketch, "E450", {"start": v(-26.17, -11.2) * mm, "end": v(-26.27, -11.19) * mm});
            skLineSegment(sketch, "E451", {"start": v(-26.27, -11.19) * mm, "end": v(-26.3, -11.18) * mm});
            skLineSegment(sketch, "E452", {"start": v(-26.3, -11.18) * mm, "end": v(-26.34, -11.17) * mm});
            skLineSegment(sketch, "E453", {"start": v(-26.34, -11.17) * mm, "end": v(-26.36, -11.16) * mm});
            skLineSegment(sketch, "E454", {"start": v(-26.36, -11.16) * mm, "end": v(-26.39, -11.15) * mm});
            skLineSegment(sketch, "E455", {"start": v(-26.39, -11.15) * mm, "end": v(-26.41, -11.13) * mm});
            skLineSegment(sketch, "E456", {"start": v(-26.41, -11.13) * mm, "end": v(-26.43, -11.11) * mm});
            skLineSegment(sketch, "E457", {"start": v(-26.43, -11.11) * mm, "end": v(-26.46, -11.1) * mm});
            skLineSegment(sketch, "E458", {"start": v(-26.46, -11.1) * mm, "end": v(-26.47, -11.08) * mm});
            skLineSegment(sketch, "E459", {"start": v(-26.47, -11.08) * mm, "end": v(-26.5, -11.05) * mm});
            skLineSegment(sketch, "E460", {"start": v(-26.5, -11.05) * mm, "end": v(-26.5, -11.03) * mm});
            skLineSegment(sketch, "E461", {"start": v(-26.5, -11.03) * mm, "end": v(-26.52, -11) * mm});
            skLineSegment(sketch, "E462", {"start": v(-26.52, -11) * mm, "end": v(-26.54, -10.98) * mm});
            skLineSegment(sketch, "E463", {"start": v(-26.54, -10.98) * mm, "end": v(-26.55, -10.95) * mm});
            skLineSegment(sketch, "E464", {"start": v(-26.55, -10.95) * mm, "end": v(-26.56, -10.93) * mm});
            skLineSegment(sketch, "E465", {"start": v(-26.56, -10.93) * mm, "end": v(-26.57, -10.9) * mm});
            skLineSegment(sketch, "E466", {"start": v(-26.57, -10.9) * mm, "end": v(-26.58, -10.87) * mm});
            skLineSegment(sketch, "E467", {"start": v(-26.58, -10.87) * mm, "end": v(-26.59, -10.84) * mm});
            skLineSegment(sketch, "E468", {"start": v(-26.59, -10.84) * mm, "end": v(-26.6, -10.78) * mm});
            skLineSegment(sketch, "E469", {"start": v(-26.6, -10.78) * mm, "end": v(-26.61, -10.72) * mm});
            skLineSegment(sketch, "E470", {"start": v(-26.61, -10.72) * mm, "end": v(-26.62, -10.63) * mm});
            skLineSegment(sketch, "E471", {"start": v(-26.62, -10.63) * mm, "end": v(-26.63, -10.55) * mm});
            skLineSegment(sketch, "E472", {"start": v(-26.63, -10.55) * mm, "end": v(-26.63, -10.5) * mm});
            skLineSegment(sketch, "E473", {"start": v(-26.63, -10.5) * mm, "end": v(-26.63, -10.47) * mm});
            skLineSegment(sketch, "E474", {"start": v(-26.63, -10.47) * mm, "end": v(-26.63, -10.38) * mm});
            skLineSegment(sketch, "E475", {"start": v(-26.63, -10.38) * mm, "end": v(-26.62, -10.23) * mm});
            skLineSegment(sketch, "E476", {"start": v(-26.62, -10.23) * mm, "end": v(-26.62, -10.14) * mm});
            skLineSegment(sketch, "E477", {"start": v(-26.62, -10.14) * mm, "end": v(-26.6, -10.08) * mm});
            skLineSegment(sketch, "E478", {"start": v(-26.6, -10.08) * mm, "end": v(-26.6, -10.02) * mm});
            skLineSegment(sketch, "E479", {"start": v(-26.6, -10.02) * mm, "end": v(-26.59, -9.99) * mm});
            skLineSegment(sketch, "E480", {"start": v(-26.59, -9.99) * mm, "end": v(-26.58, -9.96) * mm});
            skLineSegment(sketch, "E481", {"start": v(-26.58, -9.96) * mm, "end": v(-26.57, -9.93) * mm});
            skLineSegment(sketch, "E482", {"start": v(-26.57, -9.93) * mm, "end": v(-26.56, -9.9) * mm});
            skLineSegment(sketch, "E483", {"start": v(-26.56, -9.9) * mm, "end": v(-26.55, -9.87) * mm});
            skLineSegment(sketch, "E484", {"start": v(-26.55, -9.87) * mm, "end": v(-26.54, -9.85) * mm});
            skLineSegment(sketch, "E485", {"start": v(-26.54, -9.85) * mm, "end": v(-26.52, -9.82) * mm});
            skLineSegment(sketch, "E486", {"start": v(-26.52, -9.82) * mm, "end": v(-26.5, -9.8) * mm});
            skLineSegment(sketch, "E487", {"start": v(-26.5, -9.8) * mm, "end": v(-26.49, -9.77) * mm});
            skLineSegment(sketch, "E488", {"start": v(-26.49, -9.77) * mm, "end": v(-26.47, -9.75) * mm});
            skLineSegment(sketch, "E489", {"start": v(-26.47, -9.75) * mm, "end": v(-26.45, -9.73) * mm});
            skLineSegment(sketch, "E490", {"start": v(-26.45, -9.73) * mm, "end": v(-26.43, -9.71) * mm});
            skLineSegment(sketch, "E491", {"start": v(-26.43, -9.71) * mm, "end": v(-26.4, -9.7) * mm});
            skLineSegment(sketch, "E492", {"start": v(-26.4, -9.7) * mm, "end": v(-26.38, -9.67) * mm});
            skLineSegment(sketch, "E493", {"start": v(-7.73, -9.64) * mm, "end": v(-6.54, -9.67) * mm});
            skLineSegment(sketch, "E494", {"start": v(-6.54, -9.67) * mm, "end": v(-6.51, -9.75) * mm});
            skLineSegment(sketch, "E495", {"start": v(-6.51, -9.75) * mm, "end": v(-6.48, -9.83) * mm});
            skLineSegment(sketch, "E496", {"start": v(-6.48, -9.83) * mm, "end": v(-6.46, -9.9) * mm});
            skLineSegment(sketch, "E497", {"start": v(-6.46, -9.9) * mm, "end": v(-6.44, -9.99) * mm});
            skLineSegment(sketch, "E498", {"start": v(-6.44, -9.99) * mm, "end": v(-6.42, -10.07) * mm});
            skLineSegment(sketch, "E499", {"start": v(-6.42, -10.07) * mm, "end": v(-6.4, -10.15) * mm});
            skLineSegment(sketch, "E500", {"start": v(-6.4, -10.15) * mm, "end": v(-6.4, -10.23) * mm});
            skLineSegment(sketch, "E501", {"start": v(-6.4, -10.23) * mm, "end": v(-6.39, -10.32) * mm});
            skLineSegment(sketch, "E502", {"start": v(-6.39, -10.32) * mm, "end": v(-6.38, -10.4) * mm});
            skLineSegment(sketch, "E503", {"start": v(-6.38, -10.4) * mm, "end": v(-6.38, -10.44) * mm});
            skLineSegment(sketch, "E504", {"start": v(-6.38, -10.44) * mm, "end": v(-6.38, -10.48) * mm});
            skLineSegment(sketch, "E505", {"start": v(-6.38, -10.48) * mm, "end": v(-6.38, -10.53) * mm});
            skLineSegment(sketch, "E506", {"start": v(-6.38, -10.53) * mm, "end": v(-6.39, -10.57) * mm});
            skLineSegment(sketch, "E507", {"start": v(-6.39, -10.57) * mm, "end": v(-6.39, -10.6) * mm});
            skLineSegment(sketch, "E508", {"start": v(-6.39, -10.6) * mm, "end": v(-6.4, -10.65) * mm});
            skLineSegment(sketch, "E509", {"start": v(-6.4, -10.65) * mm, "end": v(-6.4, -10.7) * mm});
            skLineSegment(sketch, "E510", {"start": v(-6.4, -10.7) * mm, "end": v(-6.4, -10.73) * mm});
            skLineSegment(sketch, "E511", {"start": v(-6.4, -10.73) * mm, "end": v(-6.41, -10.77) * mm});
            skLineSegment(sketch, "E512", {"start": v(-6.41, -10.77) * mm, "end": v(-6.42, -10.82) * mm});
            skLineSegment(sketch, "E513", {"start": v(-6.42, -10.82) * mm, "end": v(-6.43, -10.86) * mm});
            skLineSegment(sketch, "E514", {"start": v(-6.43, -10.86) * mm, "end": v(-6.45, -10.92) * mm});
            skLineSegment(sketch, "E515", {"start": v(-6.45, -10.92) * mm, "end": v(-6.47, -10.97) * mm});
            skLineSegment(sketch, "E516", {"start": v(-6.47, -10.97) * mm, "end": v(-6.5, -11.03) * mm});
            skLineSegment(sketch, "E517", {"start": v(-6.5, -11.03) * mm, "end": v(-6.53, -11.07) * mm});
            skLineSegment(sketch, "E518", {"start": v(-6.53, -11.07) * mm, "end": v(-6.56, -11.1) * mm});
            skLineSegment(sketch, "E519", {"start": v(-6.56, -11.1) * mm, "end": v(-6.58, -11.12) * mm});
            skLineSegment(sketch, "E520", {"start": v(-6.58, -11.12) * mm, "end": v(-6.6, -11.14) * mm});
            skLineSegment(sketch, "E521", {"start": v(-6.6, -11.14) * mm, "end": v(-6.64, -11.15) * mm});
            skLineSegment(sketch, "E522", {"start": v(-6.64, -11.15) * mm, "end": v(-6.66, -11.17) * mm});
            skLineSegment(sketch, "E523", {"start": v(-6.66, -11.17) * mm, "end": v(-6.7, -11.18) * mm});
            skLineSegment(sketch, "E524", {"start": v(-6.7, -11.18) * mm, "end": v(-6.7, -11.18) * mm});
            skLineSegment(sketch, "E525", {"start": v(-6.7, -11.18) * mm, "end": v(-7.72, -11.2) * mm});
            skLineSegment(sketch, "E526", {"start": v(-7.72, -11.2) * mm, "end": v(-7.73, -9.64) * mm});
            skLineSegment(sketch, "E527", {"start": v(-26.47, -12.01) * mm, "end": v(-25.28, -11.98) * mm});
            skLineSegment(sketch, "E528", {"start": v(-25.28, -11.98) * mm, "end": v(-25.3, -13.53) * mm});
            skLineSegment(sketch, "E529", {"start": v(-25.3, -13.53) * mm, "end": v(-25.33, -13.53) * mm});
            skLineSegment(sketch, "E530", {"start": v(-25.33, -13.53) * mm, "end": v(-25.38, -13.52) * mm});
            skLineSegment(sketch, "E531", {"start": v(-25.38, -13.52) * mm, "end": v(-25.42, -13.52) * mm});
            skLineSegment(sketch, "E532", {"start": v(-25.42, -13.52) * mm, "end": v(-25.47, -13.52) * mm});
            skLineSegment(sketch, "E533", {"start": v(-25.47, -13.52) * mm, "end": v(-25.5, -13.52) * mm});
            skLineSegment(sketch, "E534", {"start": v(-25.5, -13.52) * mm, "end": v(-25.6, -13.53) * mm});
            skLineSegment(sketch, "E535", {"start": v(-25.6, -13.53) * mm, "end": v(-25.88, -13.56) * mm});
            skLineSegment(sketch, "E536", {"start": v(-25.88, -13.56) * mm, "end": v(-25.93, -13.56) * mm});
            skLineSegment(sketch, "E537", {"start": v(-25.93, -13.56) * mm, "end": v(-25.97, -13.56) * mm});
            skLineSegment(sketch, "E538", {"start": v(-25.97, -13.56) * mm, "end": v(-26.02, -13.56) * mm});
            skLineSegment(sketch, "E539", {"start": v(-26.02, -13.56) * mm, "end": v(-26.06, -13.56) * mm});
            skLineSegment(sketch, "E540", {"start": v(-26.06, -13.56) * mm, "end": v(-26.1, -13.56) * mm});
            skLineSegment(sketch, "E541", {"start": v(-26.1, -13.56) * mm, "end": v(-26.15, -13.56) * mm});
            skLineSegment(sketch, "E542", {"start": v(-26.15, -13.56) * mm, "end": v(-26.2, -13.55) * mm});
            skLineSegment(sketch, "E543", {"start": v(-26.2, -13.55) * mm, "end": v(-26.24, -13.54) * mm});
            skLineSegment(sketch, "E544", {"start": v(-26.24, -13.54) * mm, "end": v(-26.28, -13.53) * mm});
            skLineSegment(sketch, "E545", {"start": v(-26.28, -13.53) * mm, "end": v(-26.32, -13.52) * mm});
            skLineSegment(sketch, "E546", {"start": v(-26.32, -13.52) * mm, "end": v(-26.36, -13.5) * mm});
            skLineSegment(sketch, "E547", {"start": v(-26.36, -13.5) * mm, "end": v(-26.4, -13.48) * mm});
            skLineSegment(sketch, "E548", {"start": v(-26.4, -13.48) * mm, "end": v(-26.43, -13.45) * mm});
            skLineSegment(sketch, "E549", {"start": v(-26.43, -13.45) * mm, "end": v(-26.46, -13.43) * mm});
            skLineSegment(sketch, "E550", {"start": v(-26.46, -13.43) * mm, "end": v(-26.5, -13.4) * mm});
            skLineSegment(sketch, "E551", {"start": v(-26.5, -13.4) * mm, "end": v(-26.53, -13.36) * mm});
            skLineSegment(sketch, "E552", {"start": v(-26.53, -13.36) * mm, "end": v(-26.55, -13.31) * mm});
            skLineSegment(sketch, "E553", {"start": v(-26.55, -13.31) * mm, "end": v(-26.56, -13.27) * mm});
            skLineSegment(sketch, "E554", {"start": v(-26.56, -13.27) * mm, "end": v(-26.57, -13.22) * mm});
            skLineSegment(sketch, "E555", {"start": v(-26.57, -13.22) * mm, "end": v(-26.59, -13.18) * mm});
            skLineSegment(sketch, "E556", {"start": v(-26.59, -13.18) * mm, "end": v(-26.6, -13.13) * mm});
            skLineSegment(sketch, "E557", {"start": v(-26.6, -13.13) * mm, "end": v(-26.6, -13.08) * mm});
            skLineSegment(sketch, "E558", {"start": v(-26.6, -13.08) * mm, "end": v(-26.61, -13.04) * mm});
            skLineSegment(sketch, "E559", {"start": v(-26.61, -13.04) * mm, "end": v(-26.62, -12.99) * mm});
            skLineSegment(sketch, "E560", {"start": v(-26.62, -12.99) * mm, "end": v(-26.63, -12.94) * mm});
            skLineSegment(sketch, "E561", {"start": v(-26.63, -12.94) * mm, "end": v(-26.63, -12.9) * mm});
            skLineSegment(sketch, "E562", {"start": v(-26.63, -12.9) * mm, "end": v(-26.63, -12.85) * mm});
            skLineSegment(sketch, "E563", {"start": v(-26.63, -12.85) * mm, "end": v(-26.63, -12.8) * mm});
            skLineSegment(sketch, "E564", {"start": v(-26.63, -12.8) * mm, "end": v(-26.63, -12.75) * mm});
            skLineSegment(sketch, "E565", {"start": v(-26.63, -12.75) * mm, "end": v(-26.63, -12.7) * mm});
            skLineSegment(sketch, "E566", {"start": v(-26.63, -12.7) * mm, "end": v(-26.63, -12.66) * mm});
            skLineSegment(sketch, "E567", {"start": v(-26.63, -12.66) * mm, "end": v(-26.62, -12.6) * mm});
            skLineSegment(sketch, "E568", {"start": v(-26.62, -12.6) * mm, "end": v(-26.62, -12.56) * mm});
            skLineSegment(sketch, "E569", {"start": v(-26.62, -12.56) * mm, "end": v(-26.61, -12.51) * mm});
            skLineSegment(sketch, "E570", {"start": v(-26.61, -12.51) * mm, "end": v(-26.6, -12.47) * mm});
            skLineSegment(sketch, "E571", {"start": v(-26.6, -12.47) * mm, "end": v(-26.6, -12.42) * mm});
            skLineSegment(sketch, "E572", {"start": v(-26.6, -12.42) * mm, "end": v(-26.59, -12.37) * mm});
            skLineSegment(sketch, "E573", {"start": v(-26.59, -12.37) * mm, "end": v(-26.58, -12.33) * mm});
            skLineSegment(sketch, "E574", {"start": v(-26.58, -12.33) * mm, "end": v(-26.56, -12.28) * mm});
            skLineSegment(sketch, "E575", {"start": v(-26.56, -12.28) * mm, "end": v(-26.55, -12.23) * mm});
            skLineSegment(sketch, "E576", {"start": v(-26.55, -12.23) * mm, "end": v(-26.54, -12.19) * mm});
            skLineSegment(sketch, "E577", {"start": v(-26.54, -12.19) * mm, "end": v(-26.52, -12.14) * mm});
            skLineSegment(sketch, "E578", {"start": v(-26.52, -12.14) * mm, "end": v(-26.5, -12.1) * mm});
            skLineSegment(sketch, "E579", {"start": v(-26.5, -12.1) * mm, "end": v(-26.49, -12.05) * mm});
            skLineSegment(sketch, "E580", {"start": v(-26.49, -12.05) * mm, "end": v(-26.47, -12.01) * mm});
            skLineSegment(sketch, "E581", {"start": v(-7.73, -11.98) * mm, "end": v(-6.54, -12.01) * mm});
            skLineSegment(sketch, "E582", {"start": v(-6.54, -12.01) * mm, "end": v(-6.52, -12.06) * mm});
            skLineSegment(sketch, "E583", {"start": v(-6.52, -12.06) * mm, "end": v(-6.5, -12.1) * mm});
            skLineSegment(sketch, "E584", {"start": v(-6.5, -12.1) * mm, "end": v(-6.49, -12.16) * mm});
            skLineSegment(sketch, "E585", {"start": v(-6.49, -12.16) * mm, "end": v(-6.47, -12.2) * mm});
            skLineSegment(sketch, "E586", {"start": v(-6.47, -12.2) * mm, "end": v(-6.46, -12.26) * mm});
            skLineSegment(sketch, "E587", {"start": v(-6.46, -12.26) * mm, "end": v(-6.44, -12.31) * mm});
            skLineSegment(sketch, "E588", {"start": v(-6.44, -12.31) * mm, "end": v(-6.43, -12.37) * mm});
            skLineSegment(sketch, "E589", {"start": v(-6.43, -12.37) * mm, "end": v(-6.42, -12.42) * mm});
            skLineSegment(sketch, "E590", {"start": v(-6.42, -12.42) * mm, "end": v(-6.4, -12.48) * mm});
            skLineSegment(sketch, "E591", {"start": v(-6.4, -12.48) * mm, "end": v(-6.4, -12.53) * mm});
            skLineSegment(sketch, "E592", {"start": v(-6.4, -12.53) * mm, "end": v(-6.39, -12.59) * mm});
            skLineSegment(sketch, "E593", {"start": v(-6.39, -12.59) * mm, "end": v(-6.38, -12.64) * mm});
            skLineSegment(sketch, "E594", {"start": v(-6.38, -12.64) * mm, "end": v(-6.38, -12.7) * mm});
            skLineSegment(sketch, "E595", {"start": v(-6.38, -12.7) * mm, "end": v(-6.37, -12.75) * mm});
            skLineSegment(sketch, "E596", {"start": v(-6.37, -12.75) * mm, "end": v(-6.37, -12.8) * mm});
            skLineSegment(sketch, "E597", {"start": v(-6.37, -12.8) * mm, "end": v(-6.37, -12.86) * mm});
            skLineSegment(sketch, "E598", {"start": v(-6.37, -12.86) * mm, "end": v(-6.38, -12.91) * mm});
            skLineSegment(sketch, "E599", {"start": v(-6.38, -12.91) * mm, "end": v(-6.38, -12.97) * mm});
            skLineSegment(sketch, "E600", {"start": v(-6.38, -12.97) * mm, "end": v(-6.39, -13.02) * mm});
            skLineSegment(sketch, "E601", {"start": v(-6.39, -13.02) * mm, "end": v(-6.4, -13.07) * mm});
            skLineSegment(sketch, "E602", {"start": v(-6.4, -13.07) * mm, "end": v(-6.4, -13.12) * mm});
            skLineSegment(sketch, "E603", {"start": v(-6.4, -13.12) * mm, "end": v(-6.42, -13.17) * mm});
            skLineSegment(sketch, "E604", {"start": v(-6.42, -13.17) * mm, "end": v(-6.44, -13.22) * mm});
            skLineSegment(sketch, "E605", {"start": v(-6.44, -13.22) * mm, "end": v(-6.46, -13.27) * mm});
            skLineSegment(sketch, "E606", {"start": v(-6.46, -13.27) * mm, "end": v(-6.49, -13.32) * mm});
            skLineSegment(sketch, "E607", {"start": v(-6.49, -13.32) * mm, "end": v(-6.51, -13.36) * mm});
            skLineSegment(sketch, "E608", {"start": v(-6.51, -13.36) * mm, "end": v(-6.54, -13.4) * mm});
            skLineSegment(sketch, "E609", {"start": v(-6.54, -13.4) * mm, "end": v(-6.58, -13.45) * mm});
            skLineSegment(sketch, "E610", {"start": v(-6.58, -13.45) * mm, "end": v(-6.61, -13.49) * mm});
            skLineSegment(sketch, "E611", {"start": v(-6.61, -13.49) * mm, "end": v(-6.65, -13.5) * mm});
            skLineSegment(sketch, "E612", {"start": v(-6.65, -13.5) * mm, "end": v(-6.69, -13.5) * mm});
            skLineSegment(sketch, "E613", {"start": v(-6.69, -13.5) * mm, "end": v(-6.72, -13.52) * mm});
            skLineSegment(sketch, "E614", {"start": v(-6.72, -13.52) * mm, "end": v(-6.76, -13.52) * mm});
            skLineSegment(sketch, "E615", {"start": v(-6.76, -13.52) * mm, "end": v(-6.8, -13.53) * mm});
            skLineSegment(sketch, "E616", {"start": v(-6.8, -13.53) * mm, "end": v(-6.87, -13.54) * mm});
            skLineSegment(sketch, "E617", {"start": v(-6.87, -13.54) * mm, "end": v(-6.95, -13.55) * mm});
            skLineSegment(sketch, "E618", {"start": v(-6.95, -13.55) * mm, "end": v(-7.06, -13.55) * mm});
            skLineSegment(sketch, "E619", {"start": v(-7.06, -13.55) * mm, "end": v(-7.6, -13.53) * mm});
            skLineSegment(sketch, "E620", {"start": v(-7.6, -13.53) * mm, "end": v(-7.72, -13.53) * mm});
            skLineSegment(sketch, "E621", {"start": v(-7.72, -13.53) * mm, "end": v(-7.73, -11.98) * mm});
            skLineSegment(sketch, "E622", {"start": v(-20.77, -15.27) * mm, "end": v(-19.21, -15.27) * mm});
            skLineSegment(sketch, "E623", {"start": v(-19.21, -15.27) * mm, "end": v(-19.21, -16.13) * mm});
            skLineSegment(sketch, "E624", {"start": v(-19.21, -16.13) * mm, "end": v(-19.22, -16.27) * mm});
            skLineSegment(sketch, "E625", {"start": v(-19.22, -16.27) * mm, "end": v(-19.23, -16.29) * mm});
            skLineSegment(sketch, "E626", {"start": v(-19.23, -16.29) * mm, "end": v(-19.23, -16.3) * mm});
            skLineSegment(sketch, "E627", {"start": v(-19.23, -16.3) * mm, "end": v(-19.24, -16.32) * mm});
            skLineSegment(sketch, "E628", {"start": v(-19.24, -16.32) * mm, "end": v(-19.24, -16.34) * mm});
            skLineSegment(sketch, "E629", {"start": v(-19.24, -16.34) * mm, "end": v(-19.25, -16.35) * mm});
            skLineSegment(sketch, "E630", {"start": v(-19.25, -16.35) * mm, "end": v(-19.26, -16.37) * mm});
            skLineSegment(sketch, "E631", {"start": v(-19.26, -16.37) * mm, "end": v(-19.27, -16.38) * mm});
            skLineSegment(sketch, "E632", {"start": v(-19.27, -16.38) * mm, "end": v(-19.28, -16.4) * mm});
            skLineSegment(sketch, "E633", {"start": v(-19.28, -16.4) * mm, "end": v(-19.3, -16.41) * mm});
            skLineSegment(sketch, "E634", {"start": v(-19.3, -16.41) * mm, "end": v(-19.32, -16.43) * mm});
            skLineSegment(sketch, "E635", {"start": v(-19.32, -16.43) * mm, "end": v(-19.34, -16.46) * mm});
            skLineSegment(sketch, "E636", {"start": v(-19.34, -16.46) * mm, "end": v(-19.39, -16.49) * mm});
            skLineSegment(sketch, "E637", {"start": v(-19.39, -16.49) * mm, "end": v(-19.47, -16.53) * mm});
            skLineSegment(sketch, "E638", {"start": v(-19.47, -16.53) * mm, "end": v(-19.6, -16.58) * mm});
            skLineSegment(sketch, "E639", {"start": v(-19.6, -16.58) * mm, "end": v(-19.69, -16.6) * mm});
            skLineSegment(sketch, "E640", {"start": v(-19.69, -16.6) * mm, "end": v(-19.73, -16.6) * mm});
            skLineSegment(sketch, "E641", {"start": v(-19.73, -16.6) * mm, "end": v(-19.77, -16.6) * mm});
            skLineSegment(sketch, "E642", {"start": v(-19.77, -16.6) * mm, "end": v(-19.81, -16.61) * mm});
            skLineSegment(sketch, "E643", {"start": v(-19.81, -16.61) * mm, "end": v(-19.86, -16.62) * mm});
            skLineSegment(sketch, "E644", {"start": v(-19.86, -16.62) * mm, "end": v(-19.9, -16.62) * mm});
            skLineSegment(sketch, "E645", {"start": v(-19.9, -16.62) * mm, "end": v(-19.94, -16.62) * mm});
            skLineSegment(sketch, "E646", {"start": v(-19.94, -16.62) * mm, "end": v(-19.98, -16.62) * mm});
            skLineSegment(sketch, "E647", {"start": v(-19.98, -16.62) * mm, "end": v(-20.03, -16.62) * mm});
            skLineSegment(sketch, "E648", {"start": v(-20.03, -16.62) * mm, "end": v(-20.07, -16.62) * mm});
            skLineSegment(sketch, "E649", {"start": v(-20.07, -16.62) * mm, "end": v(-20.11, -16.62) * mm});
            skLineSegment(sketch, "E650", {"start": v(-20.11, -16.62) * mm, "end": v(-20.15, -16.62) * mm});
            skLineSegment(sketch, "E651", {"start": v(-20.15, -16.62) * mm, "end": v(-20.2, -16.61) * mm});
            skLineSegment(sketch, "E652", {"start": v(-20.2, -16.61) * mm, "end": v(-20.24, -16.6) * mm});
            skLineSegment(sketch, "E653", {"start": v(-20.24, -16.6) * mm, "end": v(-20.28, -16.6) * mm});
            skLineSegment(sketch, "E654", {"start": v(-20.28, -16.6) * mm, "end": v(-20.32, -16.6) * mm});
            skLineSegment(sketch, "E655", {"start": v(-20.32, -16.6) * mm, "end": v(-20.36, -16.58) * mm});
            skLineSegment(sketch, "E656", {"start": v(-20.36, -16.58) * mm, "end": v(-20.4, -16.57) * mm});
            skLineSegment(sketch, "E657", {"start": v(-20.4, -16.57) * mm, "end": v(-20.44, -16.56) * mm});
            skLineSegment(sketch, "E658", {"start": v(-20.44, -16.56) * mm, "end": v(-20.48, -16.54) * mm});
            skLineSegment(sketch, "E659", {"start": v(-20.48, -16.54) * mm, "end": v(-20.52, -16.53) * mm});
            skLineSegment(sketch, "E660", {"start": v(-20.52, -16.53) * mm, "end": v(-20.56, -16.51) * mm});
            skLineSegment(sketch, "E661", {"start": v(-20.56, -16.51) * mm, "end": v(-20.6, -16.5) * mm});
            skLineSegment(sketch, "E662", {"start": v(-20.6, -16.5) * mm, "end": v(-20.64, -16.47) * mm});
            skLineSegment(sketch, "E663", {"start": v(-20.64, -16.47) * mm, "end": v(-20.68, -16.45) * mm});
            skLineSegment(sketch, "E664", {"start": v(-20.68, -16.45) * mm, "end": v(-20.71, -16.43) * mm});
            skLineSegment(sketch, "E665", {"start": v(-20.71, -16.43) * mm, "end": v(-20.75, -16.4) * mm});
            skLineSegment(sketch, "E666", {"start": v(-20.75, -16.4) * mm, "end": v(-20.78, -16.38) * mm});
            skLineSegment(sketch, "E667", {"start": v(-20.78, -16.38) * mm, "end": v(-20.77, -15.27) * mm});
            skLineSegment(sketch, "E668", {"start": v(-18.48, -15.27) * mm, "end": v(-16.91, -15.27) * mm});
            skLineSegment(sketch, "E669", {"start": v(-16.91, -15.27) * mm, "end": v(-16.89, -16.15) * mm});
            skLineSegment(sketch, "E670", {"start": v(-16.89, -16.15) * mm, "end": v(-16.9, -16.21) * mm});
            skLineSegment(sketch, "E671", {"start": v(-16.9, -16.21) * mm, "end": v(-16.9, -16.27) * mm});
            skLineSegment(sketch, "E672", {"start": v(-16.9, -16.27) * mm, "end": v(-16.93, -16.32) * mm});
            skLineSegment(sketch, "E673", {"start": v(-16.93, -16.32) * mm, "end": v(-16.96, -16.37) * mm});
            skLineSegment(sketch, "E674", {"start": v(-16.96, -16.37) * mm, "end": v(-17, -16.42) * mm});
            skLineSegment(sketch, "E675", {"start": v(-17, -16.42) * mm, "end": v(-17.02, -16.45) * mm});
            skLineSegment(sketch, "E676", {"start": v(-17.02, -16.45) * mm, "end": v(-17.04, -16.47) * mm});
            skLineSegment(sketch, "E677", {"start": v(-17.04, -16.47) * mm, "end": v(-17.07, -16.5) * mm});
            skLineSegment(sketch, "E678", {"start": v(-17.07, -16.5) * mm, "end": v(-17.1, -16.52) * mm});
            skLineSegment(sketch, "E679", {"start": v(-17.1, -16.52) * mm, "end": v(-17.13, -16.54) * mm});
            skLineSegment(sketch, "E680", {"start": v(-17.13, -16.54) * mm, "end": v(-17.15, -16.55) * mm});
            skLineSegment(sketch, "E681", {"start": v(-17.15, -16.55) * mm, "end": v(-17.17, -16.56) * mm});
            skLineSegment(sketch, "E682", {"start": v(-17.17, -16.56) * mm, "end": v(-17.19, -16.56) * mm});
            skLineSegment(sketch, "E683", {"start": v(-17.19, -16.56) * mm, "end": v(-17.2, -16.57) * mm});
            skLineSegment(sketch, "E684", {"start": v(-17.2, -16.57) * mm, "end": v(-17.22, -16.57) * mm});
            skLineSegment(sketch, "E685", {"start": v(-17.22, -16.57) * mm, "end": v(-17.24, -16.57) * mm});
            skLineSegment(sketch, "E686", {"start": v(-17.24, -16.57) * mm, "end": v(-17.26, -16.58) * mm});
            skLineSegment(sketch, "E687", {"start": v(-17.26, -16.58) * mm, "end": v(-17.3, -16.58) * mm});
            skLineSegment(sketch, "E688", {"start": v(-17.3, -16.58) * mm, "end": v(-17.39, -16.6) * mm});
            skLineSegment(sketch, "E689", {"start": v(-17.39, -16.6) * mm, "end": v(-17.47, -16.61) * mm});
            skLineSegment(sketch, "E690", {"start": v(-17.47, -16.61) * mm, "end": v(-17.56, -16.62) * mm});
            skLineSegment(sketch, "E691", {"start": v(-17.56, -16.62) * mm, "end": v(-17.6, -16.62) * mm});
            skLineSegment(sketch, "E692", {"start": v(-17.6, -16.62) * mm, "end": v(-17.65, -16.63) * mm});
            skLineSegment(sketch, "E693", {"start": v(-17.65, -16.63) * mm, "end": v(-17.7, -16.63) * mm});
            skLineSegment(sketch, "E694", {"start": v(-17.7, -16.63) * mm, "end": v(-17.74, -16.63) * mm});
            skLineSegment(sketch, "E695", {"start": v(-17.74, -16.63) * mm, "end": v(-17.79, -16.63) * mm});
            skLineSegment(sketch, "E696", {"start": v(-17.79, -16.63) * mm, "end": v(-17.83, -16.62) * mm});
            skLineSegment(sketch, "E697", {"start": v(-17.83, -16.62) * mm, "end": v(-17.88, -16.62) * mm});
            skLineSegment(sketch, "E698", {"start": v(-17.88, -16.62) * mm, "end": v(-17.92, -16.61) * mm});
            skLineSegment(sketch, "E699", {"start": v(-17.92, -16.61) * mm, "end": v(-17.96, -16.6) * mm});
            skLineSegment(sketch, "E700", {"start": v(-17.96, -16.6) * mm, "end": v(-18, -16.6) * mm});
            skLineSegment(sketch, "E701", {"start": v(-18, -16.6) * mm, "end": v(-18.05, -16.59) * mm});
            skLineSegment(sketch, "E702", {"start": v(-18.05, -16.59) * mm, "end": v(-18.1, -16.57) * mm});
            skLineSegment(sketch, "E703", {"start": v(-18.1, -16.57) * mm, "end": v(-18.13, -16.56) * mm});
            skLineSegment(sketch, "E704", {"start": v(-18.13, -16.56) * mm, "end": v(-18.17, -16.54) * mm});
            skLineSegment(sketch, "E705", {"start": v(-18.17, -16.54) * mm, "end": v(-18.2, -16.52) * mm});
            skLineSegment(sketch, "E706", {"start": v(-18.2, -16.52) * mm, "end": v(-18.25, -16.5) * mm});
            skLineSegment(sketch, "E707", {"start": v(-18.25, -16.5) * mm, "end": v(-18.28, -16.48) * mm});
            skLineSegment(sketch, "E708", {"start": v(-18.28, -16.48) * mm, "end": v(-18.32, -16.45) * mm});
            skLineSegment(sketch, "E709", {"start": v(-18.32, -16.45) * mm, "end": v(-18.35, -16.42) * mm});
            skLineSegment(sketch, "E710", {"start": v(-18.35, -16.42) * mm, "end": v(-18.38, -16.39) * mm});
            skLineSegment(sketch, "E711", {"start": v(-18.38, -16.39) * mm, "end": v(-18.4, -16.35) * mm});
            skLineSegment(sketch, "E712", {"start": v(-18.4, -16.35) * mm, "end": v(-18.44, -16.32) * mm});
            skLineSegment(sketch, "E713", {"start": v(-18.44, -16.32) * mm, "end": v(-18.45, -16.25) * mm});
            skLineSegment(sketch, "E714", {"start": v(-18.45, -16.25) * mm, "end": v(-18.46, -16.14) * mm});
            skLineSegment(sketch, "E715", {"start": v(-18.46, -16.14) * mm, "end": v(-18.48, -15.96) * mm});
            skLineSegment(sketch, "E716", {"start": v(-18.48, -15.96) * mm, "end": v(-18.48, -15.27) * mm});
            skLineSegment(sketch, "E717", {"start": v(-16.1, -15.27) * mm, "end": v(-14.53, -15.27) * mm});
            skLineSegment(sketch, "E718", {"start": v(-14.53, -15.27) * mm, "end": v(-14.53, -15.99) * mm});
            skLineSegment(sketch, "E719", {"start": v(-14.53, -15.99) * mm, "end": v(-14.54, -16.16) * mm});
            skLineSegment(sketch, "E720", {"start": v(-14.54, -16.16) * mm, "end": v(-14.55, -16.26) * mm});
            skLineSegment(sketch, "E721", {"start": v(-14.55, -16.26) * mm, "end": v(-14.57, -16.3) * mm});
            skLineSegment(sketch, "E722", {"start": v(-14.57, -16.3) * mm, "end": v(-14.59, -16.33) * mm});
            skLineSegment(sketch, "E723", {"start": v(-14.59, -16.33) * mm, "end": v(-14.6, -16.36) * mm});
            skLineSegment(sketch, "E724", {"start": v(-14.6, -16.36) * mm, "end": v(-14.63, -16.38) * mm});
            skLineSegment(sketch, "E725", {"start": v(-14.63, -16.38) * mm, "end": v(-14.65, -16.41) * mm});
            skLineSegment(sketch, "E726", {"start": v(-14.65, -16.41) * mm, "end": v(-14.67, -16.44) * mm});
            skLineSegment(sketch, "E727", {"start": v(-14.67, -16.44) * mm, "end": v(-14.7, -16.46) * mm});
            skLineSegment(sketch, "E728", {"start": v(-14.7, -16.46) * mm, "end": v(-14.73, -16.48) * mm});
            skLineSegment(sketch, "E729", {"start": v(-14.73, -16.48) * mm, "end": v(-14.76, -16.5) * mm});
            skLineSegment(sketch, "E730", {"start": v(-14.76, -16.5) * mm, "end": v(-14.78, -16.52) * mm});
            skLineSegment(sketch, "E731", {"start": v(-14.78, -16.52) * mm, "end": v(-14.82, -16.53) * mm});
            skLineSegment(sketch, "E732", {"start": v(-14.82, -16.53) * mm, "end": v(-14.85, -16.55) * mm});
            skLineSegment(sketch, "E733", {"start": v(-14.85, -16.55) * mm, "end": v(-14.88, -16.56) * mm});
            skLineSegment(sketch, "E734", {"start": v(-14.88, -16.56) * mm, "end": v(-14.91, -16.57) * mm});
            skLineSegment(sketch, "E735", {"start": v(-14.91, -16.57) * mm, "end": v(-14.95, -16.58) * mm});
            skLineSegment(sketch, "E736", {"start": v(-14.95, -16.58) * mm, "end": v(-14.98, -16.59) * mm});
            skLineSegment(sketch, "E737", {"start": v(-14.98, -16.59) * mm, "end": v(-15.02, -16.6) * mm});
            skLineSegment(sketch, "E738", {"start": v(-15.02, -16.6) * mm, "end": v(-15.05, -16.6) * mm});
            skLineSegment(sketch, "E739", {"start": v(-15.05, -16.6) * mm, "end": v(-15.1, -16.6) * mm});
            skLineSegment(sketch, "E740", {"start": v(-15.1, -16.6) * mm, "end": v(-15.16, -16.61) * mm});
            skLineSegment(sketch, "E741", {"start": v(-15.16, -16.61) * mm, "end": v(-15.24, -16.62) * mm});
            skLineSegment(sketch, "E742", {"start": v(-15.24, -16.62) * mm, "end": v(-15.3, -16.62) * mm});
            skLineSegment(sketch, "E743", {"start": v(-15.3, -16.62) * mm, "end": v(-15.38, -16.62) * mm});
            skLineSegment(sketch, "E744", {"start": v(-15.38, -16.62) * mm, "end": v(-15.44, -16.61) * mm});
            skLineSegment(sketch, "E745", {"start": v(-15.44, -16.61) * mm, "end": v(-15.5, -16.62) * mm});
            skLineSegment(sketch, "E746", {"start": v(-15.5, -16.62) * mm, "end": v(-15.55, -16.61) * mm});
            skLineSegment(sketch, "E747", {"start": v(-15.55, -16.61) * mm, "end": v(-15.6, -16.6) * mm});
            skLineSegment(sketch, "E748", {"start": v(-15.6, -16.6) * mm, "end": v(-15.66, -16.6) * mm});
            skLineSegment(sketch, "E749", {"start": v(-15.66, -16.6) * mm, "end": v(-15.71, -16.59) * mm});
            skLineSegment(sketch, "E750", {"start": v(-15.71, -16.59) * mm, "end": v(-15.74, -16.58) * mm});
            skLineSegment(sketch, "E751", {"start": v(-15.74, -16.58) * mm, "end": v(-15.77, -16.57) * mm});
            skLineSegment(sketch, "E752", {"start": v(-15.77, -16.57) * mm, "end": v(-15.8, -16.56) * mm});
            skLineSegment(sketch, "E753", {"start": v(-15.8, -16.56) * mm, "end": v(-15.82, -16.55) * mm});
            skLineSegment(sketch, "E754", {"start": v(-15.82, -16.55) * mm, "end": v(-15.84, -16.54) * mm});
            skLineSegment(sketch, "E755", {"start": v(-15.84, -16.54) * mm, "end": v(-15.87, -16.53) * mm});
            skLineSegment(sketch, "E756", {"start": v(-15.87, -16.53) * mm, "end": v(-15.9, -16.52) * mm});
            skLineSegment(sketch, "E757", {"start": v(-15.9, -16.52) * mm, "end": v(-15.92, -16.5) * mm});
            skLineSegment(sketch, "E758", {"start": v(-15.92, -16.5) * mm, "end": v(-15.94, -16.49) * mm});
            skLineSegment(sketch, "E759", {"start": v(-15.94, -16.49) * mm, "end": v(-15.96, -16.47) * mm});
            skLineSegment(sketch, "E760", {"start": v(-15.96, -16.47) * mm, "end": v(-15.98, -16.46) * mm});
            skLineSegment(sketch, "E761", {"start": v(-15.98, -16.46) * mm, "end": v(-16, -16.44) * mm});
            skLineSegment(sketch, "E762", {"start": v(-16, -16.44) * mm, "end": v(-16.02, -16.42) * mm});
            skLineSegment(sketch, "E763", {"start": v(-16.02, -16.42) * mm, "end": v(-16.04, -16.4) * mm});
            skLineSegment(sketch, "E764", {"start": v(-16.04, -16.4) * mm, "end": v(-16.05, -16.38) * mm});
            skLineSegment(sketch, "E765", {"start": v(-16.05, -16.38) * mm, "end": v(-16.07, -16.35) * mm});
            skLineSegment(sketch, "E766", {"start": v(-16.07, -16.35) * mm, "end": v(-16.08, -16.33) * mm});
            skLineSegment(sketch, "E767", {"start": v(-16.08, -16.33) * mm, "end": v(-16.1, -16.3) * mm});
            skLineSegment(sketch, "E768", {"start": v(-16.1, -16.3) * mm, "end": v(-16.1, -16.28) * mm});
            skLineSegment(sketch, "E769", {"start": v(-16.1, -16.28) * mm, "end": v(-16.12, -16.18) * mm});
            skLineSegment(sketch, "E770", {"start": v(-16.12, -16.18) * mm, "end": v(-16.13, -16.04) * mm});
            skLineSegment(sketch, "E771", {"start": v(-16.13, -16.04) * mm, "end": v(-16.13, -15.76) * mm});
            skLineSegment(sketch, "E772", {"start": v(-16.13, -15.76) * mm, "end": v(-16.1, -15.27) * mm});
            skLineSegment(sketch, "E773", {"start": v(-13.8, -15.27) * mm, "end": v(-12.24, -15.27) * mm});
            skLineSegment(sketch, "E774", {"start": v(-12.24, -15.27) * mm, "end": v(-12.23, -16.38) * mm});
            skLineSegment(sketch, "E775", {"start": v(-12.23, -16.38) * mm, "end": v(-12.27, -16.4) * mm});
            skLineSegment(sketch, "E776", {"start": v(-12.27, -16.4) * mm, "end": v(-12.3, -16.43) * mm});
            skLineSegment(sketch, "E777", {"start": v(-12.3, -16.43) * mm, "end": v(-12.34, -16.45) * mm});
            skLineSegment(sketch, "E778", {"start": v(-12.34, -16.45) * mm, "end": v(-12.38, -16.48) * mm});
            skLineSegment(sketch, "E779", {"start": v(-12.38, -16.48) * mm, "end": v(-12.42, -16.5) * mm});
            skLineSegment(sketch, "E780", {"start": v(-12.42, -16.5) * mm, "end": v(-12.46, -16.51) * mm});
            skLineSegment(sketch, "E781", {"start": v(-12.46, -16.51) * mm, "end": v(-12.5, -16.53) * mm});
            skLineSegment(sketch, "E782", {"start": v(-12.5, -16.53) * mm, "end": v(-12.54, -16.55) * mm});
            skLineSegment(sketch, "E783", {"start": v(-12.54, -16.55) * mm, "end": v(-12.58, -16.56) * mm});
            skLineSegment(sketch, "E784", {"start": v(-12.58, -16.56) * mm, "end": v(-12.62, -16.57) * mm});
            skLineSegment(sketch, "E785", {"start": v(-12.62, -16.57) * mm, "end": v(-12.66, -16.58) * mm});
            skLineSegment(sketch, "E786", {"start": v(-12.66, -16.58) * mm, "end": v(-12.7, -16.6) * mm});
            skLineSegment(sketch, "E787", {"start": v(-12.7, -16.6) * mm, "end": v(-12.75, -16.6) * mm});
            skLineSegment(sketch, "E788", {"start": v(-12.75, -16.6) * mm, "end": v(-12.8, -16.6) * mm});
            skLineSegment(sketch, "E789", {"start": v(-12.8, -16.6) * mm, "end": v(-12.84, -16.61) * mm});
            skLineSegment(sketch, "E790", {"start": v(-12.84, -16.61) * mm, "end": v(-12.88, -16.62) * mm});
            skLineSegment(sketch, "E791", {"start": v(-12.88, -16.62) * mm, "end": v(-12.92, -16.62) * mm});
            skLineSegment(sketch, "E792", {"start": v(-12.92, -16.62) * mm, "end": v(-12.97, -16.62) * mm});
            skLineSegment(sketch, "E793", {"start": v(-12.97, -16.62) * mm, "end": v(-13.01, -16.62) * mm});
            skLineSegment(sketch, "E794", {"start": v(-13.01, -16.62) * mm, "end": v(-13.05, -16.62) * mm});
            skLineSegment(sketch, "E795", {"start": v(-13.05, -16.62) * mm, "end": v(-13.1, -16.62) * mm});
            skLineSegment(sketch, "E796", {"start": v(-13.1, -16.62) * mm, "end": v(-13.14, -16.62) * mm});
            skLineSegment(sketch, "E797", {"start": v(-13.14, -16.62) * mm, "end": v(-13.19, -16.61) * mm});
            skLineSegment(sketch, "E798", {"start": v(-13.19, -16.61) * mm, "end": v(-13.23, -16.6) * mm});
            skLineSegment(sketch, "E799", {"start": v(-13.23, -16.6) * mm, "end": v(-13.27, -16.6) * mm});
            skLineSegment(sketch, "E800", {"start": v(-13.27, -16.6) * mm, "end": v(-13.32, -16.6) * mm});
            skLineSegment(sketch, "E801", {"start": v(-13.32, -16.6) * mm, "end": v(-13.36, -16.59) * mm});
            skLineSegment(sketch, "E802", {"start": v(-13.36, -16.59) * mm, "end": v(-13.4, -16.58) * mm});
            skLineSegment(sketch, "E803", {"start": v(-13.4, -16.58) * mm, "end": v(-13.44, -16.57) * mm});
            skLineSegment(sketch, "E804", {"start": v(-13.44, -16.57) * mm, "end": v(-13.63, -16.48) * mm});
            skLineSegment(sketch, "E805", {"start": v(-13.63, -16.48) * mm, "end": v(-13.67, -16.46) * mm});
            skLineSegment(sketch, "E806", {"start": v(-13.67, -16.46) * mm, "end": v(-13.7, -16.44) * mm});
            skLineSegment(sketch, "E807", {"start": v(-13.7, -16.44) * mm, "end": v(-13.72, -16.42) * mm});
            skLineSegment(sketch, "E808", {"start": v(-13.72, -16.42) * mm, "end": v(-13.74, -16.4) * mm});
            skLineSegment(sketch, "E809", {"start": v(-13.74, -16.4) * mm, "end": v(-13.74, -16.39) * mm});
            skLineSegment(sketch, "E810", {"start": v(-13.74, -16.39) * mm, "end": v(-13.75, -16.37) * mm});
            skLineSegment(sketch, "E811", {"start": v(-13.75, -16.37) * mm, "end": v(-13.76, -16.36) * mm});
            skLineSegment(sketch, "E812", {"start": v(-13.76, -16.36) * mm, "end": v(-13.76, -16.34) * mm});
            skLineSegment(sketch, "E813", {"start": v(-13.76, -16.34) * mm, "end": v(-13.77, -16.33) * mm});
            skLineSegment(sketch, "E814", {"start": v(-13.77, -16.33) * mm, "end": v(-13.77, -16.31) * mm});
            skLineSegment(sketch, "E815", {"start": v(-13.77, -16.31) * mm, "end": v(-13.78, -16.3) * mm});
            skLineSegment(sketch, "E816", {"start": v(-13.78, -16.3) * mm, "end": v(-13.8, -15.27) * mm});
            skFitSpline(sketch, "E817", {"points": [v(-16.09, 0.4) * mm, v(-16.48, 0.53) * mm, v(-16.87, 0.42) * mm], "startDerivative": vector(-0.77, 0.4) * mm, "endDerivative": vector(-0.8, -0.36) * mm});
            skFitSpline(sketch, "E818", {"points": [v(-9.68, -1.66) * mm, v(-8.41, -1.95) * mm, v(-8.04, -3.41) * mm], "startDerivative": vector(3.1, -0.07) * mm, "endDerivative": vector(0.22, -3.4) * mm});
            skLineSegment(sketch, "E819", {"start": v(-8.04, -3.41) * mm, "end": v(-8.04, -3.57) * mm});
            skLineSegment(sketch, "E820", {"start": v(-16.09, 0.4) * mm, "end": v(-15.75, 0.24) * mm});
            skLineSegment(sketch, "E821", {"start": v(-17.01, 0.36) * mm, "end": v(-16.87, 0.42) * mm});
            skLineSegment(sketch, "E822", {"start": v(-9.68, -1.66) * mm, "end": v(-9.7, 0.57) * mm});
            skLineSegment(sketch, "E823", {"start": v(-13.9, -1.75) * mm, "end": v(-16.26, -0.55) * mm});
            skFitSpline(sketch, "E824", {"points": [v(-16.26, -0.55) * mm, v(-16.5, -0.47) * mm, v(-16.83, -0.6) * mm], "startDerivative": vector(-0.52, 0.27) * mm, "endDerivative": vector(-0.63, -0.37) * mm});
            skFitSpline(sketch, "E825", {"points": [v(-9.4, -3.99) * mm, v(-9.18, -4.2) * mm, v(-9.85, -4.84) * mm], "startDerivative": vector(0.88, -0.52) * mm, "endDerivative": vector(-1.57, -1.12) * mm});
            skSolve(sketch);
        }
        {
            var Q0;
            Q0=qSketchRegion(id+"F27",true);
            extrude(context, id + "F28", {"entities" : qUnion([Q0]), "operationType" : NewBodyOperationType.ADD, "depth" : 26.5 * mm});
        }
        {
            var Q0;
            Q0=qSketchRegion(id+"F27",true);
            var Q1;
            {var subQ0=sQuery(id+"F0.wireOp",EDGE,"E7.rect.top");var subQ1=sQuery(id+"F0.wireOp",EDGE,"E7.rect.right");var subQ2=sQuery(id+"F0.wireOp",EDGE,"E7.rect.left");var subQ3=sQuery(id+"F0.wireOp",EDGE,"E7.rect.bottom");var subQ4=sQuery(id+"F0.wireOp",EDGE,"E5.MirrorC");var subQ5=sQuery(id+"F0.wireOp",EDGE,"E3");var subQ6=sQuery(id+"F0.wireOp",EDGE,"E2");var subQ7=sQuery(id+"F0.wireOp",EDGE,"E1");Q1=makeQuery(id+"F28.boolean.opBoolean","SPLIT",FACE,{"disambiguationData":[TD([makeQuery(id+"F28.opExtrude","SWEPT_FACE",FACE,{"disambiguationData":[OSD([sQuery(id+"F27.wireOp",EDGE,"E90")])]})])],"derivedFrom":makeQuery(id+"F6.opShell","OFFSET_FACE",FACE,{"disambiguationData":[OSD([subQ7,subQ6,subQ5,subQ4,subQ3,subQ0,subQ2,subQ1]),TDD([makeQuery(id+"F1.opExtrude","CAP_FACE",FACE,{"disambiguationData":[OSD([subQ7,subQ6,subQ5,subQ4,subQ3,subQ0,subQ2,subQ1])],"isStart":false})])]})});}
            extrude(context, id + "F29", {"entities" : qUnion([Q0]), "operationType" : NewBodyOperationType.REMOVE, "endBound" : BoundingType.UP_TO_SURFACE, "endBoundEntityFace" : qUnion([Q1]), "depth" : 23 * mm});
        }
        {
            var Q0;
            {var subQ0=sQuery(id+"F18.wireOp",EDGE,"E51");Q0=makeQuery(id+"F18.imprint","IMPRINT",FACE,{"disambiguationData":[TD([[makeQuery(id+"F18.imprint","IMPRINT",EDGE,{"derivedFrom":subQ0}),-1.0]])]});}
            extrude(context, id + "F30", {"entities" : qUnion([Q0]), "operationType" : NewBodyOperationType.REMOVE, "oppositeDirection" : true, "depth" : 2 * mm});
        }
        {
            var Q0;
            Q0=qCreatedBy(makeId("Top.planeOp"),FACE);
            var sketch = newSketch(context, id + "F31", { "sketchPlane" : qUnion([Q0])});
            skLineSegment(sketch, "E826.rect.bottom", {"start": v(14.55, -7.47) * mm, "end": v(6.95, -7.47) * mm});
            skLineSegment(sketch, "E826.rect.top", {"start": v(14.55, -7.07) * mm, "end": v(6.95, -7.07) * mm});
            skLineSegment(sketch, "E826.rect.left", {"start": v(14.55, -7.47) * mm, "end": v(14.55, -7.07) * mm});
            skLineSegment(sketch, "E826.rect.right", {"start": v(6.95, -7.47) * mm, "end": v(6.95, -7.07) * mm});
            skPoint(sketch, "E826.rect.middle", {"position": v(10.75, -7.27) * mm});
            skSolve(sketch);
        }
        {
            var Q0;
            Q0=qSketchRegion(id+"F31",true);
            var Q1;
            Q1=makeQuery(id+"F6.opShell","OFFSET_FACE",FACE,{"disambiguationData":[OSD([sQuery(id+"F2.wireOp",EDGE,"E16")])]});
            extrude(context, id + "F32", {"entities" : qUnion([Q0]), "operationType" : NewBodyOperationType.ADD, "endBound" : BoundingType.UP_TO_SURFACE, "endBoundEntityFace" : qUnion([Q1]), "depth" : 25 * mm});
        }
        {
            var Q0;
            {var subQ0=sQuery(id+"F0.wireOp",EDGE,"E7.rect.top");var subQ1=sQuery(id+"F0.wireOp",EDGE,"E7.rect.right");var subQ2=sQuery(id+"F0.wireOp",EDGE,"E7.rect.left");var subQ3=sQuery(id+"F0.wireOp",EDGE,"E7.rect.bottom");var subQ4=sQuery(id+"F0.wireOp",EDGE,"E5.MirrorC");var subQ5=sQuery(id+"F0.wireOp",EDGE,"E3");var subQ6=sQuery(id+"F0.wireOp",EDGE,"E2");var subQ7=sQuery(id+"F0.wireOp",EDGE,"E1");Q0=makeQuery(id+"F28.boolean.opBoolean","SPLIT",FACE,{"disambiguationData":[TD([makeQuery(id+"F4.opFillet","BLEND_FACE",FACE,{"disambiguationData":[OSD([subQ0])]})])],"derivedFrom":makeQuery(id+"F1.opExtrude","CAP_FACE",FACE,{"disambiguationData":[OSD([subQ7,subQ6,subQ5,subQ4,subQ3,subQ0,subQ2,subQ1])],"isStart":false})});}
            cPlane(context, id + "F33", {"entities" : qUnion([Q0]), "cplaneType" : CPlaneType.OFFSET, "offset" : 9 * mm, "oppositeDirection" : true, "width" : 150 * mm, "height" : 150 * mm});
        }
        {
            var Q0;
            Q0=qCreatedBy(id+"F33.planeOp",FACE);
            var sketch = newSketch(context, id + "F34", { "sketchPlane" : qUnion([Q0])});
            skCircle(sketch, "E827", {"center": v(-29.86, -30.9) * mm, "radius": 1.22 * mm});
            skCircle(sketch, "E828", {"center": v(-29.84, 14.65) * mm, "radius": 1.25 * mm});
            skSolve(sketch);
        }
        {
            var Q0;
            Q0=qSketchRegion(id+"F34",true);
            var Q1;
            Q1=makeQuery(id+"F3.boolean.opBoolean","COPY",FACE,{"derivedFrom":makeQuery(id+"F3.opExtrude","SWEPT_FACE",FACE,{"disambiguationData":[OSD([sQuery(id+"F2.wireOp",EDGE,"E14")])]})});
            extrude(context, id + "F35", {"entities" : qUnion([Q0]), "operationType" : NewBodyOperationType.ADD, "endBound" : BoundingType.UP_TO_SURFACE, "endBoundEntityFace" : qUnion([Q1]), "depth" : 25 * mm});
        }
        {
            var Q0;
            {var subQ0=sQuery(id+"F0.wireOp",EDGE,"E7.rect.right");var subQ1=sQuery(id+"F0.wireOp",EDGE,"E7.rect.left");var subQ2=sQuery(id+"F0.wireOp",EDGE,"E7.rect.top");var subQ3=sQuery(id+"F0.wireOp",EDGE,"E7.rect.bottom");var subQ4=sQuery(id+"F0.wireOp",EDGE,"E5.MirrorC");var subQ5=sQuery(id+"F0.wireOp",EDGE,"E3");var subQ6=sQuery(id+"F0.wireOp",EDGE,"E2");var subQ7=sQuery(id+"F0.wireOp",EDGE,"E1");Q0=makeQuery(id+"F28.boolean.opBoolean","SPLIT",FACE,{"disambiguationData":[TD([makeQuery(id+"F4.opFillet","BLEND_FACE",FACE,{"disambiguationData":[OSD([subQ3])]})])],"derivedFrom":makeQuery(id+"F1.opExtrude","CAP_FACE",FACE,{"disambiguationData":[OSD([subQ7,subQ6,subQ5,subQ4,subQ3,subQ2,subQ1,subQ0])],"isStart":false})});}
            cPlane(context, id + "F36", {"entities" : qUnion([Q0]), "cplaneType" : CPlaneType.OFFSET, "offset" : 17.5 * mm, "oppositeDirection" : true, "width" : 150 * mm, "height" : 150 * mm});
        }
        {
            var Q0;
            Q0=qCreatedBy(id+"F36.planeOp",FACE);
            var sketch = newSketch(context, id + "F37", { "sketchPlane" : qUnion([Q0])});
            skCircle(sketch, "E829", {"center": v(8.9, 3.98) * mm, "radius": 1.26 * mm});
            skCircle(sketch, "E830", {"center": v(15.8, -30.92) * mm, "radius": 1.17 * mm});
            skSolve(sketch);
        }
        {
            var Q0;
            Q0=qSketchRegion(id+"F37",true);
            var Q1;
            Q1=makeQuery(id+"F3.boolean.opBoolean","COPY",FACE,{"derivedFrom":makeQuery(id+"F3.opExtrude","SWEPT_FACE",FACE,{"disambiguationData":[OSD([sQuery(id+"F2.wireOp",EDGE,"E16")])]})});
            extrude(context, id + "F38", {"entities" : qUnion([Q0]), "operationType" : NewBodyOperationType.ADD, "endBound" : BoundingType.UP_TO_SURFACE, "endBoundEntityFace" : qUnion([Q1]), "depth" : 25 * mm});
        }
    });
